FREECAD ASSEMBLY — COMPONENT RECIPES ("Assembly")

This assembly document has 5 components, labeled P0..P4 below (a component is one placed body or linked part). 5 of them carry a construction recipe — the FreeCAD feature program that regenerates the part from scratch, quoted from this document or its linked companion documents; the rest are supplied as boundary geometry only. No exploded tour is included for this assembly.
COMPONENT P0 — recipe-attached ("Backplane_DC", a linked part whose construction recipe lives in a companion FreeCAD document of the same project; that document's serialized recipe follows).
Construction recipe (the companion document, serialized — sketch geometry with constraints, then the solid features built on it; lengths are millimeters unless a unit is written):

FCSTD DOCUMENT  (FreeCAD 1.0R39109 (Git))
Label: Backplane_DC
License: All rights reserved
LicenseURL: https://en.wikipedia.org/wiki/All_rights_reserved
objects: Part::Feature×13, App::Part×11, PartDesign::CoordinateSystem×1, Sketcher::SketchObject×1
note: 16 computed .brp shape members not serialized (recipe doc carries the construction recipe); baked Part::Feature solids carry a one-line shape summary decoded from their .brp

FEATURE [Part::Feature] Part__Feature  label="MVQ-45H_____G_20130806_"
  shape: bbox 45.7 x 25.4 x 21.51 mm, 127 faces (baked)
FEATURE [Part::Feature] Part__Feature001  label="U\.1"
  Placement = pos=(-0.5,0,0) rot=(0,0,1;0rad)
  shape: bbox 57.37 x 25.98 x 2.346 mm, 78 faces (baked)
FEATURE [Part::Feature] Part__Feature002  label="PcB"
  Placement = pos=(-0.5,0,3.7) rot=(0,0,1;0rad)
  shape: bbox 42 x 22 x 1 mm, 8 faces (baked)
FEATURE [Part::Feature] Part__Feature003  label="pin.2"
  Placement = pos=(70.2231,-12.25,2.69484) rot=(0,1,0;3.14159rad)
  shape: bbox 1.8 x 1.8 x 9.8 mm, 12 faces (baked)
FEATURE [Part::Feature] Part__Feature004  label="pin.003"
  Placement = pos=(31.7232,-9.5,2.69484) rot=(0,1,0;3.14159rad)
  shape: bbox 1.8 x 1.8 x 9.8 mm, 12 faces (baked)
FEATURE [Part::Feature] Part__Feature005  label="pin.004"
  Placement = pos=(70.2231,-20.25,2.69484) rot=(0,1,0;3.14159rad)
  shape: bbox 1.8 x 1.8 x 9.8 mm, 12 faces (baked)
FEATURE [Part::Feature] Part__Feature006  label="pin.005"
  Placement = pos=(31.7232,-20.25,2.69484) rot=(0,1,0;3.14159rad)
  shape: bbox 1.8 x 1.8 x 9.8 mm, 12 faces (baked)
FEATURE [Part::Feature] Part__Feature007  label="79fa9e9c-a09d-11ed-8f45-a0cec80452fd_part"
  shape: bbox 8.4 x 14.4 x 13.5 mm, 26 faces (baked)
FEATURE [Part::Feature] Part__Feature008  label="79faa16c-a09d-11ed-8f45-a0cec80452fd_part"
  shape: bbox 1.1 x 1.1 x 2.6 mm, 12 faces (baked)
FEATURE [Part::Feature] Part__Feature009  label="79faa16c-a09d-11ed-8f45-a0cec80452fd_part001"
  shape: bbox 1.1 x 1.1 x 2.6 mm, 12 faces (baked)
FEATURE [Part::Feature] Part__Feature010  label="79faa16c-a09d-11ed-8f45-a0cec80452fd_part002"
  shape: bbox 1.1 x 1.1 x 2.6 mm, 12 faces (baked)
FEATURE [Part::Feature] Part__Feature011  label="79faa16c-a09d-11ed-8f45-a0cec80452fd_part003"
  shape: bbox 1.1 x 1.1 x 2.6 mm, 12 faces (baked)
FEATURE [App::Part] _9fa9e9c_a09d_11ed_8f45_a0cec80452fd  label="79fa9e9c-a09d-11ed-8f45-a0cec80452fd"
  Group = -> [Part__Feature007]
  Origin = -> Origin010
FEATURE [App::Part] _9faa16c_a09d_11ed_8f45_a0cec80452fd_part  label="79faa16c-a09d-11ed-8f45-a0cec80452fd_part004"
  Group = -> [Part__Feature008,Part__Feature009,Part__Feature010,Part__Feature011]
  Origin = -> Origin011
FEATURE [App::Part] _9faa16c_a09d_11ed_8f45_a0cec80452fd  label="79faa16c-a09d-11ed-8f45-a0cec80452fd"
  Group = -> [_9faa16c_a09d_11ed_8f45_a0cec80452fd_part]
  Origin = -> Origin012
FEATURE [App::Part] _9fa99c4_a09d_11ed_8f45_a0cec80452fd  label="79fa99c4-a09d-11ed-8f45-a0cec80452fd"
  Group = -> [_9fa9e9c_a09d_11ed_8f45_a0cec80452fd,_9faa16c_a09d_11ed_8f45_a0cec80452fd]
  Origin = -> Origin013
FEATURE [App::Part] CQ_assembly  label="J1_CQ assembly_5c03a136c24c"
  Group = -> [_9fa99c4_a09d_11ed_8f45_a0cec80452fd]
  Origin = -> Origin014
  Placement = pos=(88.1,2,0) rot=(0,0,1;1.5708rad)
FEATURE [App::Part] a1
  Group = -> [Part__Feature002,Part__Feature003,Part__Feature004,Part__Feature005,Part__Feature006]
  Origin = -> Origin008
FEATURE [App::Part] a2  label="U1_a2_d1753a728807"
  Group = -> [Part__Feature,Part__Feature001,a1]
  Origin = -> Origin009
  Placement = pos=(38.35,-48.52,0) rot=(0,0,1;0rad)
FEATURE [App::Part] Top_587c
  Group = -> [a2,CQ_assembly]
  Origin = -> Origin003
FEATURE [App::Part] Step_Models_587c
  Group = -> [Top_587c]
  Origin = -> Origin002
FEATURE [PartDesign::CoordinateSystem] Local_CS_587c
  AttacherType = Attacher::AttachEngine3D
  MapMode = 2
FEATURE [Part::Feature] Pcb_587c
  Placement = pos=(-40,140,0) rot=(0,0,1;0rad)
  shape: bbox 100 x 100 x 1.6 mm, 31 faces (baked)
FEATURE [Sketcher::SketchObject] PCB_Sketch_587c
  ArcFitTolerance = 1e-06
  FullyConstrained = false
  MakeInternals = false
  sketch-geometry (4):
    g0: LineSegment StartX=0 StartY=100 StartZ=0 EndX=100 EndY=100 EndZ=0
    g1: LineSegment StartX=100 StartY=100 StartZ=0 EndX=100 EndY=0 EndZ=0
    g2: LineSegment StartX=100 StartY=0 StartZ=0 EndX=0 EndY=0 EndZ=0
    g3: LineSegment StartX=0 StartY=0 StartZ=0 EndX=0 EndY=100 EndZ=0
  constraints (4):
    c: Coincident(g2,g3)
    c: Coincident(g0,g3)
    c: Coincident(g1,g2)
    c: Coincident(g0,g1)
FEATURE [App::Part] Board_Geoms_587c
  Group = -> [Pcb_587c,PCB_Sketch_587c]
  Origin = -> Origin
FEATURE [App::Part] Board_587c  label="Backplane_DC"
  Group = -> [Step_Models_587c,Local_CS_587c,Board_Geoms_587c]
  Origin = -> Origin001
COMPONENT P1 — recipe-attached ("Filter", a linked part whose construction recipe lives in a companion FreeCAD document of the same project; that document's serialized recipe follows).
Construction recipe (the companion document, serialized — sketch geometry with constraints, then the solid features built on it; lengths are millimeters unless a unit is written):

FCSTD DOCUMENT  (FreeCAD 1.0R39109 (Git))
Label: Filter
License: All rights reserved
LicenseURL: https://en.wikipedia.org/wiki/All_rights_reserved
objects: Part::Feature×93, App::Part×13, App::Link×3, PartDesign::CoordinateSystem×1, Sketcher::SketchObject×1
note: 96 computed .brp shape members not serialized (recipe doc carries the construction recipe); baked Part::Feature solids carry a one-line shape summary decoded from their .brp

FEATURE [App::Link] J2_1_276a3e213de9_2__ln_  label="J1_1_87cd8a65c9f8[2]"
  LinkPlacement = pos=(3.5,72.922,-1.6) rot=(0.707107,-0.707107,0;3.14159rad)
  LinkedObject = -> Shape002
  Placement = pos=(3.5,72.922,-1.6) rot=(0.707107,-0.707107,0;3.14159rad)
FEATURE [App::Link] L1_76080X203_858f18e4e3ac_ln_  label="L2_76080X203_3ff0c87f3d8e"
  LinkPlacement = pos=(104.05,0,20) rot=(0.57735,-0.57735,-0.57735;2.0944rad)
  LinkedObject = -> _6080X203
  Placement = pos=(104.05,0,20) rot=(0.57735,-0.57735,-0.57735;2.0944rad)
FEATURE [Part::Feature] Part__Feature  label="76080X203 Coil and Core"
  Placement = pos=(-13.4663,17.946,63.0505) rot=(0,0,1;0rad)
  shape: bbox 55.95 x 14.35 x 55.95 mm, 14 faces (baked)
FEATURE [Part::Feature] Part__Feature001  label="76080X203 Coil and Core001"
  Placement = pos=(-13.4663,17.946,63.0505) rot=(0,0,1;0rad)
  shape: bbox 3.314 x 63.05 x 20.62 mm, 22 faces (baked)
FEATURE [Part::Feature] Part__Feature002  label="76080X203 Coil and Core002"
  Placement = pos=(-13.4663,17.946,63.0505) rot=(0,0,1;0rad)
  shape: bbox 4.92 x 53.05 x 20.42 mm, 18 faces (baked)
FEATURE [Part::Feature] Part__Feature003  label="76080X203 Coil and Core003"
  Placement = pos=(-13.4663,17.946,63.0505) rot=(0,0,1;0rad)
  shape: bbox 6.495 x 53.05 x 20.09 mm, 18 faces (baked)
FEATURE [Part::Feature] Part__Feature004  label="76080X203 Coil and Core004"
  Placement = pos=(-13.4663,17.946,63.0505) rot=(0,0,1;0rad)
  shape: bbox 8.029 x 53.05 x 19.63 mm, 18 faces (baked)
FEATURE [Part::Feature] Part__Feature005  label="76080X203 Coil and Core005"
  Placement = pos=(-13.4663,17.946,63.0505) rot=(0,0,1;0rad)
  shape: bbox 9.513 x 53.05 x 19.05 mm, 18 faces (baked)
FEATURE [Part::Feature] Part__Feature006  label="76080X203 Coil and Core006"
  Placement = pos=(-13.4663,17.946,63.0505) rot=(0,0,1;0rad)
  shape: bbox 10.94 x 53.05 x 18.36 mm, 18 faces (baked)
FEATURE [Part::Feature] Part__Feature007  label="76080X203 Coil and Core007"
  Placement = pos=(-13.4663,17.946,63.0505) rot=(0,0,1;0rad)
  shape: bbox 12.29 x 53.05 x 17.54 mm, 18 faces (baked)
FEATURE [Part::Feature] Part__Feature008  label="76080X203 Coil and Core008"
  Placement = pos=(-13.4663,17.946,63.0505) rot=(0,0,1;0rad)
  shape: bbox 13.57 x 53.05 x 16.62 mm, 18 faces (baked)
FEATURE [Part::Feature] Part__Feature009  label="76080X203 Coil and Core009"
  Placement = pos=(-13.4663,17.946,63.0505) rot=(0,0,1;0rad)
  shape: bbox 14.77 x 53.05 x 15.59 mm, 18 faces (baked)
FEATURE [Part::Feature] Part__Feature010  label="76080X203 Coil and Core010"
  Placement = pos=(-13.4663,17.946,63.0505) rot=(0,0,1;0rad)
  shape: bbox 15.87 x 53.05 x 14.47 mm, 18 faces (baked)
FEATURE [Part::Feature] Part__Feature011  label="76080X203 Coil and Core011"
  Placement = pos=(-13.4663,17.946,63.0505) rot=(0,0,1;0rad)
  shape: bbox 16.87 x 53.05 x 13.25 mm, 18 faces (baked)
FEATURE [Part::Feature] Part__Feature012  label="76080X203 Coil and Core012"
  Placement = pos=(-13.4663,17.946,63.0505) rot=(0,0,1;0rad)
  shape: bbox 17.76 x 53.05 x 11.95 mm, 18 faces (baked)
FEATURE [Part::Feature] Part__Feature013  label="76080X203 Coil and Core013"
  Placement = pos=(-13.4663,17.946,63.0505) rot=(0,0,1;0rad)
  shape: bbox 18.55 x 53.05 x 10.58 mm, 18 faces (baked)
FEATURE [Part::Feature] Part__Feature014  label="76080X203 Coil and Core014"
  Placement = pos=(-13.4663,17.946,63.0505) rot=(0,0,1;0rad)
  shape: bbox 19.21 x 53.05 x 9.136 mm, 18 faces (baked)
FEATURE [Part::Feature] Part__Feature015  label="76080X203 Coil and Core015"
  Placement = pos=(-13.4663,17.946,63.0505) rot=(0,0,1;0rad)
  shape: bbox 19.76 x 53.05 x 7.638 mm, 18 faces (baked)
FEATURE [Part::Feature] Part__Feature016  label="76080X203 Coil and Core016"
  Placement = pos=(-13.4663,17.946,63.0505) rot=(0,0,1;0rad)
  shape: bbox 20.18 x 53.05 x 6.092 mm, 18 faces (baked)
FEATURE [Part::Feature] Part__Feature017  label="76080X203 Coil and Core017"
  Placement = pos=(-13.4663,17.946,63.0505) rot=(0,0,1;0rad)
  shape: bbox 20.48 x 53.05 x 4.508 mm, 18 faces (baked)
FEATURE [Part::Feature] Part__Feature018  label="76080X203 Coil and Core018"
  Placement = pos=(-13.4663,17.946,63.0505) rot=(0,0,1;0rad)
  shape: bbox 20.65 x 53.05 x 2.896 mm, 18 faces (baked)
FEATURE [Part::Feature] Part__Feature019  label="76080X203 Coil and Core019"
  Placement = pos=(-13.4663,17.946,63.0505) rot=(0,0,1;0rad)
  shape: bbox 20.69 x 53.05 x 1.265 mm, 18 faces (baked)
FEATURE [Part::Feature] Part__Feature020  label="76080X203 Coil and Core020"
  Placement = pos=(-13.4663,17.946,63.0505) rot=(0,0,1;0rad)
  shape: bbox 20.69 x 53.05 x 1.971 mm, 18 faces (baked)
FEATURE [Part::Feature] Part__Feature021  label="76080X203 Coil and Core021"
  Placement = pos=(-13.4663,17.946,63.0505) rot=(0,0,1;0rad)
  shape: bbox 20.59 x 53.05 x 3.595 mm, 18 faces (baked)
FEATURE [Part::Feature] Part__Feature022  label="76080X203 Coil and Core022"
  Placement = pos=(-13.4663,17.946,63.0505) rot=(0,0,1;0rad)
  shape: bbox 20.37 x 53.05 x 5.196 mm, 18 faces (baked)
FEATURE [Part::Feature] Part__Feature023  label="76080X203 Coil and Core023"
  Placement = pos=(-13.4663,17.946,63.0505) rot=(0,0,1;0rad)
  shape: bbox 20.02 x 53.05 x 6.765 mm, 18 faces (baked)
FEATURE [Part::Feature] Part__Feature024  label="76080X203 Coil and Core024"
  Placement = pos=(-13.4663,17.946,63.0505) rot=(0,0,1;0rad)
  shape: bbox 19.54 x 53.05 x 8.291 mm, 18 faces (baked)
FEATURE [Part::Feature] Part__Feature025  label="76080X203 Coil and Core025"
  Placement = pos=(-13.4663,17.946,63.0505) rot=(0,0,1;0rad)
  shape: bbox 18.94 x 53.05 x 9.766 mm, 18 faces (baked)
FEATURE [Part::Feature] Part__Feature026  label="76080X203 Coil and Core026"
  Placement = pos=(-13.4663,17.946,63.0505) rot=(0,0,1;0rad)
  shape: bbox 18.22 x 53.05 x 11.18 mm, 18 faces (baked)
FEATURE [Part::Feature] Part__Feature027  label="76080X203 Coil and Core027"
  Placement = pos=(-13.4663,17.946,63.0505) rot=(0,0,1;0rad)
  shape: bbox 17.39 x 53.05 x 12.52 mm, 18 faces (baked)
FEATURE [Part::Feature] Part__Feature028  label="76080X203 Coil and Core028"
  Placement = pos=(-13.4663,17.946,63.0505) rot=(0,0,1;0rad)
  shape: bbox 16.45 x 53.05 x 13.79 mm, 18 faces (baked)
FEATURE [Part::Feature] Part__Feature029  label="76080X203 Coil and Core029"
  Placement = pos=(-13.4663,17.946,63.0505) rot=(0,0,1;0rad)
  shape: bbox 15.4 x 53.05 x 14.96 mm, 18 faces (baked)
FEATURE [Part::Feature] Part__Feature030  label="76080X203 Coil and Core030"
  Placement = pos=(-13.4663,17.946,63.0505) rot=(0,0,1;0rad)
  shape: bbox 14.26 x 53.05 x 16.05 mm, 18 faces (baked)
FEATURE [Part::Feature] Part__Feature031  label="76080X203 Coil and Core031"
  Placement = pos=(-13.4663,17.946,63.0505) rot=(0,0,1;0rad)
  shape: bbox 13.03 x 53.05 x 17.03 mm, 18 faces (baked)
FEATURE [Part::Feature] Part__Feature032  label="76080X203 Coil and Core032"
  Placement = pos=(-13.4663,17.946,63.0505) rot=(0,0,1;0rad)
  shape: bbox 11.72 x 53.05 x 17.91 mm, 18 faces (baked)
FEATURE [Part::Feature] Part__Feature033  label="76080X203 Coil and Core033"
  Placement = pos=(-13.4663,17.946,63.0505) rot=(0,0,1;0rad)
  shape: bbox 10.33 x 53.05 x 18.67 mm, 18 faces (baked)
FEATURE [Part::Feature] Part__Feature034  label="76080X203 Coil and Core034"
  Placement = pos=(-13.4663,17.946,63.0505) rot=(0,0,1;0rad)
  shape: bbox 8.879 x 53.05 x 19.32 mm, 18 faces (baked)
FEATURE [Part::Feature] Part__Feature035  label="76080X203 Coil and Core035"
  Placement = pos=(-13.4663,17.946,63.0505) rot=(0,0,1;0rad)
  shape: bbox 7.372 x 53.05 x 19.84 mm, 18 faces (baked)
FEATURE [Part::Feature] Part__Feature036  label="76080X203 Coil and Core036"
  Placement = pos=(-13.4663,17.946,63.0505) rot=(0,0,1;0rad)
  shape: bbox 5.819 x 53.05 x 20.25 mm, 18 faces (baked)
FEATURE [Part::Feature] Part__Feature037  label="76080X203 Coil and Core037"
  Placement = pos=(-13.4663,17.946,63.0505) rot=(0,0,1;0rad)
  shape: bbox 4.229 x 53.05 x 20.52 mm, 18 faces (baked)
FEATURE [Part::Feature] Part__Feature038  label="76080X203 Coil and Core038"
  Placement = pos=(-13.4663,17.946,63.0505) rot=(0,0,1;0rad)
  shape: bbox 2.613 x 53.05 x 20.67 mm, 18 faces (baked)
FEATURE [Part::Feature] Part__Feature039  label="76080X203 Coil and Core039"
  Placement = pos=(-13.4663,17.946,63.0505) rot=(0,0,1;0rad)
  shape: bbox 0.9804 x 53.05 x 20.68 mm, 18 faces (baked)
FEATURE [Part::Feature] Part__Feature040  label="76080X203 Coil and Core040"
  Placement = pos=(-13.4663,17.946,63.0505) rot=(0,0,1;0rad)
  shape: bbox 2.254 x 53.05 x 20.68 mm, 18 faces (baked)
FEATURE [Part::Feature] Part__Feature041  label="76080X203 Coil and Core041"
  Placement = pos=(-13.4663,17.946,63.0505) rot=(0,0,1;0rad)
  shape: bbox 3.875 x 53.05 x 20.56 mm, 18 faces (baked)
FEATURE [Part::Feature] Part__Feature042  label="76080X203 Coil and Core042"
  Placement = pos=(-13.4663,17.946,63.0505) rot=(0,0,1;0rad)
  shape: bbox 5.472 x 53.05 x 20.32 mm, 18 faces (baked)
FEATURE [Part::Feature] Part__Feature043  label="76080X203 Coil and Core043"
  Placement = pos=(-13.4663,17.946,63.0505) rot=(0,0,1;0rad)
  shape: bbox 7.034 x 53.05 x 19.94 mm, 18 faces (baked)
FEATURE [Part::Feature] Part__Feature044  label="76080X203 Coil and Core044"
  Placement = pos=(-13.4663,17.946,63.0505) rot=(0,0,1;0rad)
  shape: bbox 8.552 x 53.05 x 19.44 mm, 18 faces (baked)
FEATURE [Part::Feature] Part__Feature045  label="76080X203 Coil and Core045"
  Placement = pos=(-13.4663,17.946,63.0505) rot=(0,0,1;0rad)
  shape: bbox 10.02 x 53.05 x 18.82 mm, 18 faces (baked)
FEATURE [Part::Feature] Part__Feature046  label="76080X203 Coil and Core046"
  Placement = pos=(-13.4663,17.946,63.0505) rot=(0,0,1;0rad)
  shape: bbox 11.42 x 53.05 x 18.09 mm, 18 faces (baked)
FEATURE [Part::Feature] Part__Feature047  label="76080X203 Coil and Core047"
  Placement = pos=(-13.4663,17.946,63.0505) rot=(0,0,1;0rad)
  shape: bbox 12.75 x 53.05 x 17.23 mm, 18 faces (baked)
FEATURE [Part::Feature] Part__Feature048  label="76080X203 Coil and Core048"
  Placement = pos=(-13.4663,17.946,63.0505) rot=(0,0,1;0rad)
  shape: bbox 14 x 53.05 x 16.27 mm, 18 faces (baked)
FEATURE [Part::Feature] Part__Feature049  label="76080X203 Coil and Core049"
  Placement = pos=(-13.4663,17.946,63.0505) rot=(0,0,1;0rad)
  shape: bbox 15.16 x 53.05 x 15.21 mm, 18 faces (baked)
FEATURE [Part::Feature] Part__Feature050  label="76080X203 Coil and Core050"
  Placement = pos=(-13.4663,17.946,63.0505) rot=(0,0,1;0rad)
  shape: bbox 16.23 x 53.05 x 14.05 mm, 18 faces (baked)
FEATURE [Part::Feature] Part__Feature051  label="76080X203 Coil and Core051"
  Placement = pos=(-13.4663,17.946,63.0505) rot=(0,0,1;0rad)
  shape: bbox 17.19 x 53.05 x 12.81 mm, 18 faces (baked)
FEATURE [Part::Feature] Part__Feature052  label="76080X203 Coil and Core052"
  Placement = pos=(-13.4663,17.946,63.0505) rot=(0,0,1;0rad)
  shape: bbox 18.05 x 53.05 x 11.48 mm, 18 faces (baked)
FEATURE [Part::Feature] Part__Feature053  label="76080X203 Coil and Core053"
  Placement = pos=(-13.4663,17.946,63.0505) rot=(0,0,1;0rad)
  shape: bbox 18.79 x 53.05 x 10.08 mm, 18 faces (baked)
FEATURE [Part::Feature] Part__Feature054  label="76080X203 Coil and Core054"
  Placement = pos=(-13.4663,17.946,63.0505) rot=(0,0,1;0rad)
  shape: bbox 19.42 x 53.05 x 8.621 mm, 18 faces (baked)
FEATURE [Part::Feature] Part__Feature055  label="76080X203 Coil and Core055"
  Placement = pos=(-13.4663,17.946,63.0505) rot=(0,0,1;0rad)
  shape: bbox 19.92 x 53.05 x 7.105 mm, 18 faces (baked)
FEATURE [Part::Feature] Part__Feature056  label="76080X203 Coil and Core056"
  Placement = pos=(-13.4663,17.946,63.0505) rot=(0,0,1;0rad)
  shape: bbox 20.3 x 53.05 x 5.545 mm, 18 faces (baked)
FEATURE [Part::Feature] Part__Feature057  label="76080X203 Coil and Core057"
  Placement = pos=(-13.4663,17.946,63.0505) rot=(0,0,1;0rad)
  shape: bbox 20.55 x 53.05 x 3.95 mm, 18 faces (baked)
FEATURE [Part::Feature] Part__Feature058  label="76080X203 Coil and Core058"
  Placement = pos=(-13.4663,17.946,63.0505) rot=(0,0,1;0rad)
  shape: bbox 20.68 x 53.05 x 2.33 mm, 18 faces (baked)
FEATURE [Part::Feature] Part__Feature059  label="76080X203 Coil and Core059"
  Placement = pos=(-13.4663,17.946,63.0505) rot=(0,0,1;0rad)
  shape: bbox 20.68 x 53.05 x 0.9044 mm, 18 faces (baked)
FEATURE [Part::Feature] Part__Feature060  label="76080X203 Coil and Core060"
  Placement = pos=(-13.4663,17.946,63.0505) rot=(0,0,1;0rad)
  shape: bbox 20.67 x 53.05 x 2.538 mm, 18 faces (baked)
FEATURE [Part::Feature] Part__Feature061  label="76080X203 Coil and Core061"
  Placement = pos=(-13.4663,17.946,63.0505) rot=(0,0,1;0rad)
  shape: bbox 20.53 x 53.05 x 4.155 mm, 18 faces (baked)
FEATURE [Part::Feature] Part__Feature062  label="76080X203 Coil and Core062"
  Placement = pos=(-13.4663,17.946,63.0505) rot=(0,0,1;0rad)
  shape: bbox 20.26 x 53.05 x 5.746 mm, 18 faces (baked)
FEATURE [Part::Feature] Part__Feature063  label="76080X203 Coil and Core063"
  Placement = pos=(-13.4663,17.946,63.0505) rot=(0,0,1;0rad)
  shape: bbox 19.87 x 53.05 x 7.301 mm, 18 faces (baked)
FEATURE [Part::Feature] Part__Feature064  label="76080X203 Coil and Core064"
  Placement = pos=(-13.4663,17.946,63.0505) rot=(0,0,1;0rad)
  shape: bbox 19.35 x 53.05 x 8.81 mm, 18 faces (baked)
FEATURE [Part::Feature] Part__Feature065  label="76080X203 Coil and Core065"
  Placement = pos=(-13.4663,17.946,63.0505) rot=(0,0,1;0rad)
  shape: bbox 18.7 x 53.05 x 10.26 mm, 18 faces (baked)
FEATURE [Part::Feature] Part__Feature066  label="76080X203 Coil and Core066"
  Placement = pos=(-13.4663,17.946,63.0505) rot=(0,0,1;0rad)
  shape: bbox 17.95 x 53.05 x 11.65 mm, 18 faces (baked)
FEATURE [Part::Feature] Part__Feature067  label="76080X203 Coil and Core067"
  Placement = pos=(-13.4663,17.946,63.0505) rot=(0,0,1;0rad)
  shape: bbox 17.07 x 53.05 x 12.97 mm, 18 faces (baked)
FEATURE [Part::Feature] Part__Feature068  label="76080X203 Coil and Core068"
  Placement = pos=(-13.4663,17.946,63.0505) rot=(0,0,1;0rad)
  shape: bbox 16.1 x 53.05 x 14.21 mm, 18 faces (baked)
FEATURE [Part::Feature] Part__Feature069  label="76080X203 Coil and Core069"
  Placement = pos=(-13.4663,17.946,63.0505) rot=(0,0,1;0rad)
  shape: bbox 15.02 x 53.05 x 15.35 mm, 18 faces (baked)
FEATURE [Part::Feature] Part__Feature070  label="76080X203 Coil and Core070"
  Placement = pos=(-13.4663,17.946,63.0505) rot=(0,0,1;0rad)
  shape: bbox 13.84 x 53.05 x 16.4 mm, 18 faces (baked)
FEATURE [Part::Feature] Part__Feature071  label="76080X203 Coil and Core071"
  Placement = pos=(-13.4663,17.946,63.0505) rot=(0,0,1;0rad)
  shape: bbox 12.58 x 53.05 x 17.35 mm, 18 faces (baked)
FEATURE [Part::Feature] Part__Feature072  label="76080X203 Coil and Core072"
  Placement = pos=(-13.4663,17.946,63.0505) rot=(0,0,1;0rad)
  shape: bbox 11.24 x 53.05 x 18.19 mm, 18 faces (baked)
FEATURE [Part::Feature] Part__Feature073  label="76080X203 Coil and Core073"
  Placement = pos=(-13.4663,17.946,63.0505) rot=(0,0,1;0rad)
  shape: bbox 9.833 x 53.05 x 18.91 mm, 18 faces (baked)
FEATURE [Part::Feature] Part__Feature074  label="76080X203 Coil and Core074"
  Placement = pos=(-13.4663,17.946,63.0505) rot=(0,0,1;0rad)
  shape: bbox 8.361 x 53.05 x 19.52 mm, 18 faces (baked)
FEATURE [Part::Feature] Part__Feature075  label="76080X203 Coil and Core075"
  Placement = pos=(-13.4663,17.946,63.0505) rot=(0,0,1;0rad)
  shape: bbox 6.837 x 53.05 x 20 mm, 18 faces (baked)
FEATURE [Part::Feature] Part__Feature076  label="76080X203 Coil and Core076"
  Placement = pos=(-13.4663,17.946,63.0505) rot=(0,0,1;0rad)
  shape: bbox 5.27 x 53.05 x 20.36 mm, 18 faces (baked)
FEATURE [Part::Feature] Part__Feature077  label="76080X203 Coil and Core077"
  Placement = pos=(-13.4663,17.946,63.0505) rot=(0,0,1;0rad)
  shape: bbox 3.67 x 53.05 x 20.59 mm, 18 faces (baked)
FEATURE [Part::Feature] Part__Feature078  label="76080X203 Coil and Core078"
  Placement = pos=(-13.4663,17.946,63.0505) rot=(0,0,1;0rad)
  shape: bbox 1.881 x 63.05 x 20.92 mm, 22 faces (baked)
FEATURE [Part::Feature] Part__Feature079  label="76080X203 Coil and Core079"
  Placement = pos=(-13.4663,17.946,63.0505) rot=(0,0,1;0rad)
  shape: bbox 55.95 x 14.35 x 55.95 mm, 14 faces (baked)
FEATURE [Part::Feature] Part__Feature080  label="76080X203 Coil and Core080"
  Placement = pos=(-13.4663,17.946,63.0505) rot=(0,0,1;0rad)
  shape: bbox 55.95 x 14.35 x 55.95 mm, 14 faces (baked)
FEATURE [Part::Feature] Part__Feature081  label="070-7778_65mm10"
  Placement = pos=(-13.4663,39.296,63.0505) rot=(1,-0.0006,0.0006;1.5708rad)
  shape: bbox 63.86 x 10.5 x 66.59 mm, 131 faces (baked)
FEATURE [Part::Feature] Part__Feature082  label="070-7778_65mm011"
  Placement = pos=(-13.4663,-17.754,63.0505) rot=(-0.000425,0.707107,0.707107;3.14074rad)
  shape: bbox 63.86 x 10.5 x 66.59 mm, 131 faces (baked)
FEATURE [Part::Feature] Part__Feature083  label="4mm lock nut_94645A101"
  Placement = pos=(-13.4663,-13.854,63.0505) rot=(1,0,0.0006;3.14159rad)
  shape: bbox 7.082 x 0.6047 x 7.082 mm, 6 faces (baked)
FEATURE [Part::Feature] Part__Feature084  label="4mm lock nut_94645A102"
  Placement = pos=(-13.4663,-13.854,63.0505) rot=(1,0,0.0006;3.14159rad)
  shape: bbox 8.084 x 5.147 x 8.084 mm, 47 faces (baked)
FEATURE [Part::Feature] Part__Feature085  label="4mm OD 65mm long_screw_91290A083"
  Placement = pos=(-13.4663,4.39598,63.0505) rot=(-1,0,0;1.5708rad)
  shape: bbox 7.001 x 70.05 x 7.001 mm, 88 faces (baked)
FEATURE [Part::Feature] Part__Feature086  label="b59e4a84-a09d-11ed-8f45-a0cec80452fd_part"
  shape: bbox 16.8 x 24.15 x 19.6 mm, 26 faces (baked)
FEATURE [Part::Feature] Part__Feature087  label="b59e4d5e-a09d-11ed-8f45-a0cec80452fd_part"
  shape: bbox 2.1 x 2.1 x 4.6 mm, 8 faces (baked)
FEATURE [Part::Feature] Part__Feature088  label="b59e4d5e-a09d-11ed-8f45-a0cec80452fd_part001"
  shape: bbox 2.1 x 2.1 x 4.6 mm, 8 faces (baked)
FEATURE [App::Link] R1_R_Axial_DIN0617_L170mm_D60mm_P2540mm_Horizontal_f8ce5df8ddfd_ln_  label="R2_R_Axial_DIN0617_L170mm_D60mm_P2540mm_Horizontal_76c3f4d7f436"
  LinkPlacement = pos=(91,91.5,0) rot=(0,0,-1;1.5708rad)
  LinkedObject = -> Shape
  Placement = pos=(91,91.5,0) rot=(0,0,-1;1.5708rad)
FEATURE [Part::Feature] Shape  label="R1_R_Axial_DIN0617_L170mm_D60mm_P2540mm_Horizontal_f8ce5df8ddfd"
  Placement = pos=(91,31.1,0) rot=(0,0,-1;1.5708rad)
  shape: bbox 6.494 x 26.46 x 9.247 mm, 17 faces (baked)
FEATURE [Part::Feature] Shape001  label="C1_C_Rect_L265mm_W115mm_P2250mm_MKS4_fe84fe0ab4d3"
  Placement = pos=(75.6,60.95,0) rot=(0,0,-1;1.5708rad)
  shape: bbox 11.5 x 26.5 x 22.9 mm, 22 faces (baked)
FEATURE [Part::Feature] Shape002  label="J2_1_276a3e213de9[2]"
  Placement = pos=(3.5,11.962,-1.6) rot=(0.707107,-0.707107,0;3.14159rad)
  shape: bbox 7 x 4.98 x 4.98 mm, 13 faces (baked)
FEATURE [App::Part] Bot_ee73
  Group = -> [Shape002,J2_1_276a3e213de9_2__ln_]
  Origin = -> Origin004
FEATURE [App::Part] _6080X203_Coil_and_Core  label="76080X203 Coil and Core081"
  Group = -> [Part__Feature,Part__Feature001,Part__Feature002,Part__Feature003,Part__Feature004,Part__Feature005,Part__Feature006,Part__Feature007,Part__Feature008,Part__Feature009,Part__Feature010,Part__Feature011,Part__Feature012,Part__Feature013,Part__Feature014,Part__Feature015,Part__Feature016,Part__Feature017,Part__Feature018,Part__Feature019,Part__Feature020,Part__Feature021,Part__Feature022,+58 more]
  Origin = -> Origin008
FEATURE [App::Part] _mm_lock_nut_94645A101  label="4mm lock nut_94645A103"
  Group = -> [Part__Feature083,Part__Feature084]
  Origin = -> Origin009
FEATURE [App::Part] _6080X203  label="L1_76080X203_858f18e4e3ac"
  Group = -> [_6080X203_Coil_and_Core,Part__Feature081,Part__Feature082,_mm_lock_nut_94645A101,Part__Feature085]
  Origin = -> Origin010
  Placement = pos=(104.05,72.5,20) rot=(0.57735,-0.57735,-0.57735;2.0944rad)
FEATURE [App::Part] b59e4a84_a09d_11ed_8f45_a0cec80452fd  label="b59e4a84-a09d-11ed-8f45-a0cec80452fd"
  Group = -> [Part__Feature086]
  Origin = -> Origin011
FEATURE [App::Part] b59e4d5e_a09d_11ed_8f45_a0cec80452fd_part  label="b59e4d5e-a09d-11ed-8f45-a0cec80452fd_part002"
  Group = -> [Part__Feature087,Part__Feature088]
  Origin = -> Origin012
FEATURE [App::Part] b59e4d5e_a09d_11ed_8f45_a0cec80452fd  label="b59e4d5e-a09d-11ed-8f45-a0cec80452fd"
  Group = -> [b59e4d5e_a09d_11ed_8f45_a0cec80452fd_part]
  Origin = -> Origin013
FEATURE [App::Part] b59e462e_a09d_11ed_8f45_a0cec80452fd  label="b59e462e-a09d-11ed-8f45-a0cec80452fd"
  Group = -> [b59e4a84_a09d_11ed_8f45_a0cec80452fd,b59e4d5e_a09d_11ed_8f45_a0cec80452fd]
  Origin = -> Origin014
FEATURE [App::Part] CQ_assembly  label="J3_CQ assembly_8f48752883f5"
  Group = -> [b59e462e_a09d_11ed_8f45_a0cec80452fd]
  Origin = -> Origin015
  Placement = pos=(84.0925,45.85,0) rot=(0,0,1;1.5708rad)
FEATURE [App::Part] Top_ee73
  Group = -> [_6080X203,L1_76080X203_858f18e4e3ac_ln_,Shape,R1_R_Axial_DIN0617_L170mm_D60mm_P2540mm_Horizontal_f8ce5df8ddfd_ln_,Shape001,CQ_assembly]
  Origin = -> Origin003
FEATURE [App::Part] Step_Models_ee73
  Group = -> [Top_ee73,Bot_ee73]
  Origin = -> Origin002
FEATURE [PartDesign::CoordinateSystem] Local_CS_ee73
  AttacherType = Attacher::AttachEngine3D
  MapMode = 2
FEATURE [Part::Feature] Pcb_ee73
  Placement = pos=(-40,160,0) rot=(0,0,1;0rad)
  shape: bbox 100 x 100 x 1.6 mm, 44 faces (baked)
FEATURE [Sketcher::SketchObject] PCB_Sketch_ee73
  ArcFitTolerance = 1e-06
  FullyConstrained = false
  MakeInternals = false
  sketch-geometry (4):
    g0: LineSegment StartX=0 StartY=100 StartZ=0 EndX=100 EndY=100 EndZ=0
    g1: LineSegment StartX=100 StartY=100 StartZ=0 EndX=100 EndY=0 EndZ=0
    g2: LineSegment StartX=100 StartY=0 StartZ=0 EndX=0 EndY=0 EndZ=0
    g3: LineSegment StartX=0 StartY=0 StartZ=0 EndX=0 EndY=100 EndZ=0
  constraints (4):
    c: Coincident(g2,g3)
    c: Coincident(g0,g3)
    c: Coincident(g1,g2)
    c: Coincident(g0,g1)
FEATURE [App::Part] Board_Geoms_ee73
  Group = -> [Pcb_ee73,PCB_Sketch_ee73]
  Origin = -> Origin
FEATURE [App::Part] Board_ee73  label="Filter"
  Group = -> [Step_Models_ee73,Local_CS_ee73,Board_Geoms_ee73]
  Origin = -> Origin001
COMPONENT P2 — recipe-attached ("HalfBridge_SiC1", a linked part whose construction recipe lives in a companion FreeCAD document of the same project; that document's serialized recipe follows).
Construction recipe (the companion document, serialized — sketch geometry with constraints, then the solid features built on it; lengths are millimeters unless a unit is written):

FCSTD DOCUMENT  (FreeCAD 1.0R39109 (Git))
Label: HalfBridge_SiC
License: All rights reserved
LicenseURL: https://en.wikipedia.org/wiki/All_rights_reserved
objects: App::Link×105, Part::Feature×46, App::Part×15, PartDesign::CoordinateSystem×1, Sketcher::SketchObject×1
note: 49 computed .brp shape members not serialized (recipe doc carries the construction recipe); baked Part::Feature solids carry a one-line shape summary decoded from their .brp

FEATURE [PartDesign::CoordinateSystem] Local_CS_ed05
  AttacherType = Attacher::AttachEngine3D
  MapMode = 2
FEATURE [Part::Feature] Pcb_ed05
  Placement = pos=(-39.5,140.5,0) rot=(0,0,1;0rad)
  shape: bbox 100 x 100 x 1.6 mm, 113 faces (baked)
FEATURE [Sketcher::SketchObject] PCB_Sketch_ed05
  ArcFitTolerance = 1e-06
  FullyConstrained = false
  MakeInternals = false
  sketch-geometry (28):
    g0: LineSegment StartX=17.542 StartY=39.29 StartZ=0 EndX=18.542 EndY=39.29 EndZ=0
    g1: LineSegment StartX=18.542 StartY=39.29 StartZ=0 EndX=18.542 EndY=29.29 EndZ=0
    g2: LineSegment StartX=18.542 StartY=29.29 StartZ=0 EndX=17.542 EndY=29.29 EndZ=0
    g3: LineSegment StartX=17.542 StartY=29.29 StartZ=0 EndX=17.542 EndY=39.29 EndZ=0
    g4: LineSegment StartX=36.399 StartY=40.662 StartZ=0 EndX=45.383 EndY=40.662 EndZ=0
    g5: LineSegment StartX=45.383 StartY=40.662 StartZ=0 EndX=45.383 EndY=39.662 EndZ=0
    g6: LineSegment StartX=45.383 StartY=39.662 StartZ=0 EndX=36.399 EndY=39.662 EndZ=0
    g7: LineSegment StartX=36.399 StartY=39.662 StartZ=0 EndX=36.399 EndY=40.662 EndZ=0
    g8: LineSegment StartX=47.768 StartY=91.487 StartZ=0 EndX=48.514 EndY=91.487 EndZ=0
    g9: LineSegment StartX=48.514 StartY=91.487 StartZ=0 EndX=48.514 EndY=59.389 EndZ=0
    g10: LineSegment StartX=48.514 StartY=59.389 StartZ=0 EndX=47.768 EndY=59.389 EndZ=0
    g11: LineSegment StartX=47.768 StartY=59.389 StartZ=0 EndX=47.768 EndY=91.487 EndZ=0
    g12: LineSegment StartX=17.968 StartY=23.7 StartZ=0 EndX=74.68 EndY=23.7 EndZ=0
    g13: LineSegment StartX=74.68 StartY=23.7 StartZ=0 EndX=74.68 EndY=22.7 EndZ=0
    g14: LineSegment StartX=74.68 StartY=22.7 StartZ=0 EndX=17.968 EndY=22.7 EndZ=0
    g15: LineSegment StartX=17.968 StartY=22.7 StartZ=0 EndX=17.968 EndY=23.7 EndZ=0
    g16: LineSegment StartX=0 StartY=100 StartZ=0 EndX=100 EndY=100 EndZ=0
    g17: LineSegment StartX=100 StartY=100 StartZ=0 EndX=100 EndY=0 EndZ=0
    g18: LineSegment StartX=100 StartY=0 StartZ=0 EndX=0 EndY=0 EndZ=0
    g19: LineSegment StartX=0 StartY=0 StartZ=0 EndX=0 EndY=100 EndZ=0
    g20: LineSegment StartX=18.05 StartY=15.208 StartZ=0 EndX=19.05 EndY=15.208 EndZ=0
    g21: LineSegment StartX=19.05 StartY=15.208 StartZ=0 EndX=19.05 EndY=8.7 EndZ=0
    g22: LineSegment StartX=19.05 StartY=8.7 StartZ=0 EndX=18.05 EndY=8.7 EndZ=0
    g23: LineSegment StartX=18.05 StartY=8.7 StartZ=0 EndX=18.05 EndY=15.208 EndZ=0
    g24: LineSegment StartX=15.764 StartY=29.4 StartZ=0 EndX=16.764 EndY=29.4 EndZ=0
    g25: LineSegment StartX=16.764 StartY=29.4 StartZ=0 EndX=16.764 EndY=16.9 EndZ=0
    g26: LineSegment StartX=16.764 StartY=16.9 StartZ=0 EndX=15.764 EndY=16.9 EndZ=0
    g27: LineSegment StartX=15.764 StartY=16.9 StartZ=0 EndX=15.764 EndY=29.4 EndZ=0
  constraints (28):
    c: Coincident(g18,g19)
    c: Coincident(g16,g19)
    c: Coincident(g26,g27)
    c: Coincident(g24,g27)
    c: Coincident(g25,g26)
    c: Coincident(g24,g25)
    c: Coincident(g2,g3)
    c: Coincident(g0,g3)
    c: Coincident(g14,g15)
    c: Coincident(g12,g15)
    c: Coincident(g22,g23)
    c: Coincident(g20,g23)
    c: Coincident(g1,g2)
    c: Coincident(g0,g1)
    c: Coincident(g21,g22)
    c: Coincident(g20,g21)
    c: Coincident(g6,g7)
    c: Coincident(g4,g7)
    c: Coincident(g5,g6)
    c: Coincident(g4,g5)
    c: Coincident(g10,g11)
    c: Coincident(g8,g11)
    c: Coincident(g9,g10)
    c: Coincident(g8,g9)
    c: Coincident(g13,g14)
    c: Coincident(g12,g13)
    c: Coincident(g17,g18)
    c: Coincident(g16,g17)
FEATURE [App::Part] Board_Geoms_ed05
  Group = -> [Pcb_ed05,PCB_Sketch_ed05]
  Origin = -> Origin
FEATURE [Part::Feature] Shape  label="U5_SOIC-16W_7.5x10.3mm_P1.27mm_noPin12_13_606f1c37d418"
  Placement = pos=(18,23.3,0) rot=(0,0,1;0rad)
  shape: bbox 10.3 x 10.3 x 2.75 mm, 256 faces (baked)
FEATURE [Part::Feature] Shape001  label="D6_D_SOD_123_86f777a7cf57"
  Placement = pos=(31.3,17.35,0) rot=(0,0,-1;1.5708rad)
  shape: bbox 1.6 x 3.8 x 1.25 mm, 67 faces (baked)
FEATURE [Part::Feature] Shape002  label="R9_R_0603_1608Metric_fe9d9f34c5f9"
  Placement = pos=(9.9875,27.2,0) rot=(0,0,1;0rad)
  shape: bbox 1.6 x 0.8 x 0.45 mm, 26 faces (baked)
FEATURE [App::Link] D6_D_SOD_123_86f777a7cf57_ln_  label="D5_D_SOD_123_75c73be4f775"
  LinkPlacement = pos=(31.3,29.9,0) rot=(0,0,1;1.5708rad)
  LinkedObject = -> Shape001
  Placement = pos=(31.3,29.9,0) rot=(0,0,1;1.5708rad)
FEATURE [Part::Feature] Shape003  label="C15_C_0603_1608Metric_09ddd0478757"
  Placement = pos=(13.5,16.1,0) rot=(0,0,-1;1.5708rad)
  shape: bbox 0.8 x 1.6 x 0.8 mm, 28 faces (baked)
FEATURE [App::Link] C15_C_0603_1608Metric_09ddd0478757_ln_  label="C33_C_0603_1608Metric_74bc470caa33"
  LinkPlacement = pos=(9.3,80.8715,0) rot=(0,0,1;1.5708rad)
  LinkedObject = -> Shape003
  Placement = pos=(9.3,80.8715,0) rot=(0,0,1;1.5708rad)
FEATURE [Part::Feature] Shape004  label="D3_LED_0603_1608Metric_70bb5031e2ff"
  Placement = pos=(4.7,31.775,0) rot=(0,0,-1;1.5708rad)
  shape: bbox 0.8 x 1.6 x 1.1 mm, 50 faces (baked)
FEATURE [Part::Feature] Shape005  label="C38_C_0805_2012Metric_74cbd35bff10"
  Placement = pos=(6.655,73.284,0) rot=(0,0,1;0rad)
  shape: bbox 2 x 1.25 x 1.25 mm, 28 faces (baked)
FEATURE [App::Link] R9_R_0603_1608Metric_fe9d9f34c5f9_ln_  label="R33_R_0603_1608Metric_ea8747869db3"
  LinkPlacement = pos=(22.7,83.4115,0) rot=(0,0,1;1.5708rad)
  LinkedObject = -> Shape002
  Placement = pos=(22.7,83.4115,0) rot=(0,0,1;1.5708rad)
FEATURE [App::Link] C15_C_0603_1608Metric_09ddd0478757_ln_001  label="C22_C_0603_1608Metric_3b7886544036"
  LinkPlacement = pos=(25.65,28.3,0) rot=(0,0,1;0rad)
  LinkedObject = -> Shape003
  Placement = pos=(25.65,28.3,0) rot=(0,0,1;0rad)
FEATURE [Part::Feature] Part__Feature  label="CAS_c_12B"
  Placement = pos=(0,-2.4,-3e-16) rot=(0,0,1;0rad)
  shape: bbox 5.4 x 2.5 x 4.2 mm, 71 faces (baked)
FEATURE [Part::Feature] Part__Feature001  label="1 pole_s"
  Placement = pos=(0.3,-0.6,-3e-16) rot=(0,0,1;0rad)
  shape: bbox 0.6 x 0.6 x 0.7 mm, 14 faces (baked)
FEATURE [App::Part] CAS_120B1  label="SW1_CAS-120B1_eba1f44a47b7[2]"
  Group = -> [Part__Feature,Part__Feature001]
  Origin = -> Origin008
  Placement = pos=(29.242,83.058,2.5) rot=(0.57735,-0.57735,-0.57735;2.0944rad)
FEATURE [App::Link] R9_R_0603_1608Metric_fe9d9f34c5f9_ln_001  label="R14_R_0603_1608Metric_f9b5c031c635"
  LinkPlacement = pos=(28.1,36.5,0) rot=(0,0,1;1.5708rad)
  LinkedObject = -> Shape002
  Placement = pos=(28.1,36.5,0) rot=(0,0,1;1.5708rad)
FEATURE [App::Link] R9_R_0603_1608Metric_fe9d9f34c5f9_ln_002  label="R8_R_0603_1608Metric_fcb6b5fbbfd0"
  LinkPlacement = pos=(10,28.7,0) rot=(0,0,1;0rad)
  LinkedObject = -> Shape002
  Placement = pos=(10,28.7,0) rot=(0,0,1;0rad)
FEATURE [App::Link] C15_C_0603_1608Metric_09ddd0478757_ln_002  label="C45_C_0603_1608Metric_6c9f5762c5a1"
  LinkPlacement = pos=(36.9,16.256,0) rot=(0,0,1;1.5708rad)
  LinkedObject = -> Shape003
  Placement = pos=(36.9,16.256,0) rot=(0,0,1;1.5708rad)
FEATURE [App::Link] C38_C_0805_2012Metric_74cbd35bff10_ln_  label="C24_C_0805_2012Metric_4c91d95a9eef"
  LinkPlacement = pos=(25.7,8.7,0) rot=(0,0,1;3.14159rad)
  LinkedObject = -> Shape005
  Placement = pos=(25.7,8.7,0) rot=(0,0,1;3.14159rad)
FEATURE [Part::Feature] Shape006  label="U10_SOT_23_6_8cf1dc40b667"
  Placement = pos=(21.85,68.3115,0) rot=(0,0,1;3.14159rad)
  shape: bbox 2.8 x 2.9 x 1.55 mm, 124 faces (baked)
FEATURE [App::Link] C15_C_0603_1608Metric_09ddd0478757_ln_003  label="C21_C_0603_1608Metric_d16c1e161e8d"
  LinkPlacement = pos=(25.62,18.5,0) rot=(0,0,1;3.14159rad)
  LinkedObject = -> Shape003
  Placement = pos=(25.62,18.5,0) rot=(0,0,1;3.14159rad)
FEATURE [App::Link] C15_C_0603_1608Metric_09ddd0478757_ln_004  label="C42_C_0603_1608Metric_20bf4b114d9d"
  LinkPlacement = pos=(25.1,68.1115,0) rot=(0,0,1;1.5708rad)
  LinkedObject = -> Shape003
  Placement = pos=(25.1,68.1115,0) rot=(0,0,1;1.5708rad)
FEATURE [App::Link] C38_C_0805_2012Metric_74cbd35bff10_ln_001  label="C18_C_0805_2012Metric_4df3bd6c3c50"
  LinkPlacement = pos=(25.7,33.1,0) rot=(0,0,1;3.14159rad)
  LinkedObject = -> Shape005
  Placement = pos=(25.7,33.1,0) rot=(0,0,1;3.14159rad)
FEATURE [App::Link] U10_SOT_23_6_8cf1dc40b667_ln_  label="U11_SOT_23_6_c211cb7acc4a"
  LinkPlacement = pos=(21.85,58.1515,0) rot=(0,0,1;3.14159rad)
  LinkedObject = -> Shape006
  Placement = pos=(21.85,58.1515,0) rot=(0,0,1;3.14159rad)
FEATURE [App::Link] R9_R_0603_1608Metric_fe9d9f34c5f9_ln_003  label="R15_R_0603_1608Metric_55e85660f00f"
  LinkPlacement = pos=(22.6,36.1,0) rot=(0,0,-1;1.5708rad)
  LinkedObject = -> Shape002
  Placement = pos=(22.6,36.1,0) rot=(0,0,-1;1.5708rad)
FEATURE [Part::Feature] Shape007  label="R21_R_0805_2012Metric_4eff570911b6"
  Placement = pos=(34.3,28.2,0) rot=(0,0,1;0rad)
  shape: bbox 2 x 1.2 x 0.45 mm, 26 faces (baked)
FEATURE [App::Link] C15_C_0603_1608Metric_09ddd0478757_ln_005  label="C34_C_0603_1608Metric_836b7f75df63"
  LinkPlacement = pos=(9.5,60.3715,0) rot=(0,0,1;1.5708rad)
  LinkedObject = -> Shape003
  Placement = pos=(9.5,60.3715,0) rot=(0,0,1;1.5708rad)
FEATURE [App::Link] C38_C_0805_2012Metric_74cbd35bff10_ln_002  label="C39_C_0805_2012Metric_4739b33e3560"
  LinkPlacement = pos=(6.655,83.9115,0) rot=(0,0,1;0rad)
  LinkedObject = -> Shape005
  Placement = pos=(6.655,83.9115,0) rot=(0,0,1;0rad)
FEATURE [App::Link] R9_R_0603_1608Metric_fe9d9f34c5f9_ln_004  label="R16_R_0603_1608Metric_5e29ad9bbd6c"
  LinkPlacement = pos=(29.7,13.3,0) rot=(0,0,-1;1.5708rad)
  LinkedObject = -> Shape002
  Placement = pos=(29.7,13.3,0) rot=(0,0,-1;1.5708rad)
FEATURE [App::Link] C15_C_0603_1608Metric_09ddd0478757_ln_006  label="C6_C_0603_1608Metric_47ec0beeeb7c"
  LinkPlacement = pos=(36.576,85.598,0) rot=(0,0,1;0rad)
  LinkedObject = -> Shape003
  Placement = pos=(36.576,85.598,0) rot=(0,0,1;0rad)
FEATURE [App::Link] D3_LED_0603_1608Metric_70bb5031e2ff_ln_  label="D1_LED_0603_1608Metric_117d22e4d741"
  LinkPlacement = pos=(3.1,9.525,0) rot=(0,0,1;1.5708rad)
  LinkedObject = -> Shape004
  Placement = pos=(3.1,9.525,0) rot=(0,0,1;1.5708rad)
FEATURE [Part::Feature] Shape008  label="U3_SOT_23_5_e32904241429"
  Placement = pos=(34.37,62.7015,0) rot=(0,0,1;0rad)
  shape: bbox 2.8 x 2.9 x 1.55 mm, 109 faces (baked)
FEATURE [App::Link] C38_C_0805_2012Metric_74cbd35bff10_ln_003  label="C35_C_0805_2012Metric_12818f10c88b"
  LinkPlacement = pos=(7.5,67.9115,0) rot=(0,0,1;3.14159rad)
  LinkedObject = -> Shape005
  Placement = pos=(7.5,67.9115,0) rot=(0,0,1;3.14159rad)
FEATURE [Part::Feature] Shape009  label="U7_SOT_23_ed8fd63cd947"
  Placement = pos=(25.3625,36.5,0) rot=(0,0,1;3.14159rad)
  shape: bbox 2.5 x 3 x 1.2 mm, 76 faces (baked)
FEATURE [Part::Feature] Shape010  label="C5_C_2220_5750Metric_40789e461117"
  Placement = pos=(71.498,23.622,0) rot=(0,0,-1;1.5708rad)
  shape: bbox 5 x 5.7 x 2.9 mm, 28 faces (baked)
FEATURE [App::Link] R9_R_0603_1608Metric_fe9d9f34c5f9_ln_005  label="R29_R_0603_1608Metric_c415b56a8a35"
  LinkPlacement = pos=(13.655,63.4115,0) rot=(0,0,1;1.5708rad)
  LinkedObject = -> Shape002
  Placement = pos=(13.655,63.4115,0) rot=(0,0,1;1.5708rad)
FEATURE [App::Link] R9_R_0603_1608Metric_fe9d9f34c5f9_ln_006  label="R27_R_0603_1608Metric_6ecdd8c441b3"
  LinkPlacement = pos=(13.3,73.9115,0) rot=(0,0,1;1.5708rad)
  LinkedObject = -> Shape002
  Placement = pos=(13.3,73.9115,0) rot=(0,0,1;1.5708rad)
FEATURE [App::Link] R9_R_0603_1608Metric_fe9d9f34c5f9_ln_007  label="R30_R_0603_1608Metric_3d9fcfb98980"
  LinkPlacement = pos=(18.7,78.4115,0) rot=(0,0,1;1.5708rad)
  LinkedObject = -> Shape002
  Placement = pos=(18.7,78.4115,0) rot=(0,0,1;1.5708rad)
FEATURE [App::Link] C15_C_0603_1608Metric_09ddd0478757_ln_007  label="C41_C_0603_1608Metric_8a3fc6cb6ce4"
  LinkPlacement = pos=(25.1,78.4115,0) rot=(0,0,1;1.5708rad)
  LinkedObject = -> Shape003
  Placement = pos=(25.1,78.4115,0) rot=(0,0,1;1.5708rad)
FEATURE [App::Link] C5_C_2220_5750Metric_40789e461117_ln_  label="C3_C_2220_5750Metric_0b14797a19db"
  LinkPlacement = pos=(59.498,23.622,0) rot=(0,0,-1;1.5708rad)
  LinkedObject = -> Shape010
  Placement = pos=(59.498,23.622,0) rot=(0,0,-1;1.5708rad)
FEATURE [App::Link] R21_R_0805_2012Metric_4eff570911b6_ln_  label="R19_R_0805_2012Metric_5467f9f4486e"
  LinkPlacement = pos=(34.3,32.2,0) rot=(0,0,1;0rad)
  LinkedObject = -> Shape007
  Placement = pos=(34.3,32.2,0) rot=(0,0,1;0rad)
FEATURE [App::Link] C15_C_0603_1608Metric_09ddd0478757_ln_008  label="C43_C_0603_1608Metric_b35c248b52c4"
  LinkPlacement = pos=(25.1,58.1115,0) rot=(0,0,1;1.5708rad)
  LinkedObject = -> Shape003
  Placement = pos=(25.1,58.1115,0) rot=(0,0,1;1.5708rad)
FEATURE [App::Link] R21_R_0805_2012Metric_4eff570911b6_ln_001  label="R3_R_0805_2012Metric_ab16afa742b3"
  LinkPlacement = pos=(44.564,16.278,0) rot=(0,0,1;1.5708rad)
  LinkedObject = -> Shape007
  Placement = pos=(44.564,16.278,0) rot=(0,0,1;1.5708rad)
FEATURE [App::Link] R21_R_0805_2012Metric_4eff570911b6_ln_002  label="R10_R_0805_2012Metric_e1b373d5c9e0"
  LinkPlacement = pos=(8.1,18.67,0) rot=(0,0,-1;1.5708rad)
  LinkedObject = -> Shape007
  Placement = pos=(8.1,18.67,0) rot=(0,0,-1;1.5708rad)
FEATURE [App::Link] D3_LED_0603_1608Metric_70bb5031e2ff_ln_001  label="D2_LED_0603_1608Metric_72f350e39bfe"
  LinkPlacement = pos=(4.7,35.5,0) rot=(0,0,-1;1.5708rad)
  LinkedObject = -> Shape004
  Placement = pos=(4.7,35.5,0) rot=(0,0,-1;1.5708rad)
FEATURE [App::Link] R9_R_0603_1608Metric_fe9d9f34c5f9_ln_008  label="R32_R_0603_1608Metric_bd0168379d35"
  LinkPlacement = pos=(18.7,58.1115,0) rot=(0,0,1;1.5708rad)
  LinkedObject = -> Shape002
  Placement = pos=(18.7,58.1115,0) rot=(0,0,1;1.5708rad)
FEATURE [App::Link] C38_C_0805_2012Metric_74cbd35bff10_ln_004  label="C40_C_0805_2012Metric_1a8242036e69"
  LinkPlacement = pos=(6.7,63.1115,0) rot=(0,0,1;0rad)
  LinkedObject = -> Shape005
  Placement = pos=(6.7,63.1115,0) rot=(0,0,1;0rad)
FEATURE [App::Link] R21_R_0805_2012Metric_4eff570911b6_ln_003  label="R40_R_0805_2012Metric_1fb8d6502ab2"
  LinkPlacement = pos=(20.574,16.04,0) rot=(0,0,-1;1.5708rad)
  LinkedObject = -> Shape007
  Placement = pos=(20.574,16.04,0) rot=(0,0,-1;1.5708rad)
FEATURE [App::Link] C15_C_0603_1608Metric_09ddd0478757_ln_009  label="C20_C_0603_1608Metric_5de1c2e82c4e"
  LinkPlacement = pos=(25.62,21.1,0) rot=(0,0,1;0rad)
  LinkedObject = -> Shape003
  Placement = pos=(25.62,21.1,0) rot=(0,0,1;0rad)
FEATURE [App::Link] R9_R_0603_1608Metric_fe9d9f34c5f9_ln_009  label="R28_R_0603_1608Metric_db2da8ac741f"
  LinkPlacement = pos=(13.3,84.0715,0) rot=(0,0,1;1.5708rad)
  LinkedObject = -> Shape002
  Placement = pos=(13.3,84.0715,0) rot=(0,0,1;1.5708rad)
FEATURE [App::Link] C38_C_0805_2012Metric_74cbd35bff10_ln_005  label="C25_C_0805_2012Metric_d4570dd2b406"
  LinkPlacement = pos=(21.9,8.7,0) rot=(0,0,1;3.14159rad)
  LinkedObject = -> Shape005
  Placement = pos=(21.9,8.7,0) rot=(0,0,1;3.14159rad)
FEATURE [Part::Feature] Shape011  label="L5_L_0603_1608Metric_90973c27a168"
  Placement = pos=(5.1,81.1115,0) rot=(0,0,1;1.5708rad)
  shape: bbox 0.8 x 1.6 x 0.8 mm, 28 faces (baked)
FEATURE [App::Link] R21_R_0805_2012Metric_4eff570911b6_ln_004  label="R26_R_0805_2012Metric_215f856b24f5"
  LinkPlacement = pos=(34.3,13.9,0) rot=(0,0,1;0rad)
  LinkedObject = -> Shape007
  Placement = pos=(34.3,13.9,0) rot=(0,0,1;0rad)
FEATURE [App::Link] L5_L_0603_1608Metric_90973c27a168_ln_  label="L6_L_0603_1608Metric_227bb48d5cae"
  LinkPlacement = pos=(5.1,60.4265,0) rot=(0,0,1;1.5708rad)
  LinkedObject = -> Shape011
  Placement = pos=(5.1,60.4265,0) rot=(0,0,1;1.5708rad)
FEATURE [App::Link] C15_C_0603_1608Metric_09ddd0478757_ln_010  label="C14_C_0603_1608Metric_a25fa12fbfe8"
  LinkPlacement = pos=(11.3,24.6,0) rot=(0,0,-1;1.5708rad)
  LinkedObject = -> Shape003
  Placement = pos=(11.3,24.6,0) rot=(0,0,-1;1.5708rad)
FEATURE [App::Link] R9_R_0603_1608Metric_fe9d9f34c5f9_ln_010  label="R31_R_0603_1608Metric_1647f0dc400e"
  LinkPlacement = pos=(18.7,68.3115,0) rot=(0,0,1;1.5708rad)
  LinkedObject = -> Shape002
  Placement = pos=(18.7,68.3115,0) rot=(0,0,1;1.5708rad)
FEATURE [App::Link] C38_C_0805_2012Metric_74cbd35bff10_ln_006  label="C37_C_0805_2012Metric_821d07cd279f"
  LinkPlacement = pos=(7.5,57.7115,0) rot=(0,0,1;3.14159rad)
  LinkedObject = -> Shape005
  Placement = pos=(7.5,57.7115,0) rot=(0,0,1;3.14159rad)
FEATURE [App::Link] C5_C_2220_5750Metric_40789e461117_ln_001  label="C4_C_2220_5750Metric_aeb9c5b40f04"
  LinkPlacement = pos=(65.498,23.622,0) rot=(0,0,-1;1.5708rad)
  LinkedObject = -> Shape010
  Placement = pos=(65.498,23.622,0) rot=(0,0,-1;1.5708rad)
FEATURE [Part::Feature] Part__Feature002  label="CAS_c_D2B"
  Placement = pos=(0,-2.4,-3e-16) rot=(0,0,1;0rad)
  shape: bbox 5.4 x 2.5 x 5.6 mm, 110 faces (baked)
FEATURE [Part::Feature] Part__Feature003  label="Dual_s"
  Placement = pos=(0.3,-0.6,0.64) rot=(0,0,1;0rad)
  shape: bbox 0.6 x 0.6 x 0.7 mm, 14 faces (baked)
FEATURE [Part::Feature] Part__Feature004  label="Dual_s001"
  Placement = pos=(0.3,-0.6,-0.64) rot=(0,0,1;0rad)
  shape: bbox 0.6 x 0.6 x 0.7 mm, 14 faces (baked)
FEATURE [App::Part] CAS_D20B1  label="SW5_CAS-D20B1_b4c165cab9b4[2]"
  Group = -> [Part__Feature002,Part__Feature003,Part__Feature004]
  Origin = -> Origin009
  Placement = pos=(4.29,22.754,2.5) rot=(0,0.707107,0.707107;3.14159rad)
FEATURE [App::Link] R9_R_0603_1608Metric_fe9d9f34c5f9_ln_011  label="R35_R_0603_1608Metric_3c432ada0ca8"
  LinkPlacement = pos=(22.7,72.9115,0) rot=(0,0,1;1.5708rad)
  LinkedObject = -> Shape002
  Placement = pos=(22.7,72.9115,0) rot=(0,0,1;1.5708rad)
FEATURE [App::Link] U7_SOT_23_ed8fd63cd947_ln_  label="U8_SOT_23_df60fcb6f98c"
  LinkPlacement = pos=(25.3625,13.6,0) rot=(0,0,1;3.14159rad)
  LinkedObject = -> Shape009
  Placement = pos=(25.3625,13.6,0) rot=(0,0,1;3.14159rad)
FEATURE [App::Link] L5_L_0603_1608Metric_90973c27a168_ln_001  label="L4_L_0603_1608Metric_8fa15f76ae30"
  LinkPlacement = pos=(5.1,70.5865,0) rot=(0,0,1;1.5708rad)
  LinkedObject = -> Shape011
  Placement = pos=(5.1,70.5865,0) rot=(0,0,1;1.5708rad)
FEATURE [App::Link] SW1_CAS_120B1_eba1f44a47b7_2__ln_  label="SW3_CAS-120B1_d768a4589788[2]"
  LinkPlacement = pos=(29.21,62.484,2.5) rot=(0.57735,-0.57735,-0.57735;2.0944rad)
  LinkedObject = -> CAS_120B1
  Placement = pos=(29.21,62.484,2.5) rot=(0.57735,-0.57735,-0.57735;2.0944rad)
FEATURE [App::Link] C15_C_0603_1608Metric_09ddd0478757_ln_011  label="C32_C_0603_1608Metric_89b2b6ef811b"
  LinkPlacement = pos=(9.3,70.7115,0) rot=(0,0,1;1.5708rad)
  LinkedObject = -> Shape003
  Placement = pos=(9.3,70.7115,0) rot=(0,0,1;1.5708rad)
FEATURE [App::Link] C38_C_0805_2012Metric_74cbd35bff10_ln_007  label="C36_C_0805_2012Metric_4e65c6641553"
  LinkPlacement = pos=(7.9,78.1115,0) rot=(0,0,1;3.14159rad)
  LinkedObject = -> Shape005
  Placement = pos=(7.9,78.1115,0) rot=(0,0,1;3.14159rad)
FEATURE [App::Link] C5_C_2220_5750Metric_40789e461117_ln_002  label="C2_C_2220_5750Metric_dfcbf9cf85c4"
  LinkPlacement = pos=(53.498,23.622,0) rot=(0,0,-1;1.5708rad)
  LinkedObject = -> Shape010
  Placement = pos=(53.498,23.622,0) rot=(0,0,-1;1.5708rad)
FEATURE [App::Link] C15_C_0603_1608Metric_09ddd0478757_ln_012  label="C23_C_0603_1608Metric_094c659e187e"
  LinkPlacement = pos=(25.65,25.3,0) rot=(0,0,1;3.14159rad)
  LinkedObject = -> Shape003
  Placement = pos=(25.65,25.3,0) rot=(0,0,1;3.14159rad)
FEATURE [App::Link] R21_R_0805_2012Metric_4eff570911b6_ln_005  label="R20_R_0805_2012Metric_ea78c8c8eecd"
  LinkPlacement = pos=(34.3,30.2,0) rot=(0,0,1;0rad)
  LinkedObject = -> Shape007
  Placement = pos=(34.3,30.2,0) rot=(0,0,1;0rad)
FEATURE [App::Link] C38_C_0805_2012Metric_74cbd35bff10_ln_008  label="C16_C_0805_2012Metric_e5af641f3413"
  LinkPlacement = pos=(12.5,33.7,0) rot=(0,0,1;0rad)
  LinkedObject = -> Shape005
  Placement = pos=(12.5,33.7,0) rot=(0,0,1;0rad)
FEATURE [App::Link] R9_R_0603_1608Metric_fe9d9f34c5f9_ln_012  label="R34_R_0603_1608Metric_211ac095cb09"
  LinkPlacement = pos=(22.7,63.1115,0) rot=(0,0,1;1.5708rad)
  LinkedObject = -> Shape002
  Placement = pos=(22.7,63.1115,0) rot=(0,0,1;1.5708rad)
FEATURE [App::Link] C15_C_0603_1608Metric_09ddd0478757_ln_013  label="C27_C_0603_1608Metric_298082643862"
  LinkPlacement = pos=(23.6375,16.1,0) rot=(0,0,1;3.14159rad)
  LinkedObject = -> Shape003
  Placement = pos=(23.6375,16.1,0) rot=(0,0,1;3.14159rad)
FEATURE [App::Link] R21_R_0805_2012Metric_4eff570911b6_ln_006  label="R2_R_0805_2012Metric_96e20fc01cb7"
  LinkPlacement = pos=(44.564,33.296,0) rot=(0,0,1;1.5708rad)
  LinkedObject = -> Shape007
  Placement = pos=(44.564,33.296,0) rot=(0,0,1;1.5708rad)
FEATURE [App::Link] R9_R_0603_1608Metric_fe9d9f34c5f9_ln_013  label="R13_R_0603_1608Metric_df329fa1d19c"
  LinkPlacement = pos=(29.7,36.5,0) rot=(0,0,-1;1.5708rad)
  LinkedObject = -> Shape002
  Placement = pos=(29.7,36.5,0) rot=(0,0,-1;1.5708rad)
FEATURE [App::Link] U3_SOT_23_5_e32904241429_ln_  label="U2_SOT_23_5_6f2eb00efaad"
  LinkPlacement = pos=(34.37,72.8615,0) rot=(0,0,1;0rad)
  LinkedObject = -> Shape008
  Placement = pos=(34.37,72.8615,0) rot=(0,0,1;0rad)
FEATURE [App::Link] L5_L_0603_1608Metric_90973c27a168_ln_002  label="L2_L_0603_1608Metric_6584b5c4d191"
  LinkPlacement = pos=(9.3,33.1,0) rot=(0,0,-1;1.5708rad)
  LinkedObject = -> Shape011
  Placement = pos=(9.3,33.1,0) rot=(0,0,-1;1.5708rad)
FEATURE [App::Link] L5_L_0603_1608Metric_90973c27a168_ln_003  label="L3_L_0603_1608Metric_80e3bdf1ad67"
  LinkPlacement = pos=(9.3,8.7,0) rot=(0,0,1;1.5708rad)
  LinkedObject = -> Shape011
  Placement = pos=(9.3,8.7,0) rot=(0,0,1;1.5708rad)
FEATURE [App::Link] R21_R_0805_2012Metric_4eff570911b6_ln_007  label="R23_R_0805_2012Metric_772e2aabec3d"
  LinkPlacement = pos=(34.3,19.85,0) rot=(0,0,1;0rad)
  LinkedObject = -> Shape007
  Placement = pos=(34.3,19.85,0) rot=(0,0,1;0rad)
FEATURE [App::Link] C38_C_0805_2012Metric_74cbd35bff10_ln_009  label="C17_C_0805_2012Metric_9d67934c64c5"
  LinkPlacement = pos=(12.1,8.1,0) rot=(0,0,1;0rad)
  LinkedObject = -> Shape005
  Placement = pos=(12.1,8.1,0) rot=(0,0,1;0rad)
FEATURE [App::Link] U10_SOT_23_6_8cf1dc40b667_ln_001  label="U9_SOT_23_6_77935cb89beb"
  LinkPlacement = pos=(21.85,78.4715,0) rot=(0,0,1;3.14159rad)
  LinkedObject = -> Shape006
  Placement = pos=(21.85,78.4715,0) rot=(0,0,1;3.14159rad)
FEATURE [App::Link] C38_C_0805_2012Metric_74cbd35bff10_ln_010  label="C19_C_0805_2012Metric_f233b5c27be5"
  LinkPlacement = pos=(21.9,33.1,0) rot=(0,0,1;3.14159rad)
  LinkedObject = -> Shape005
  Placement = pos=(21.9,33.1,0) rot=(0,0,1;3.14159rad)
FEATURE [App::Link] SW1_CAS_120B1_eba1f44a47b7_2__ln_001  label="SW2_CAS-120B1_de4e8c04cc20[2]"
  LinkPlacement = pos=(29.242,72.898,2.5) rot=(0.57735,-0.57735,-0.57735;2.0944rad)
  LinkedObject = -> CAS_120B1
  Placement = pos=(29.242,72.898,2.5) rot=(0.57735,-0.57735,-0.57735;2.0944rad)
FEATURE [App::Link] R21_R_0805_2012Metric_4eff570911b6_ln_008  label="R25_R_0805_2012Metric_61226d1b2b79"
  LinkPlacement = pos=(34.3,15.9,0) rot=(0,0,1;0rad)
  LinkedObject = -> Shape007
  Placement = pos=(34.3,15.9,0) rot=(0,0,1;0rad)
FEATURE [App::Link] C15_C_0603_1608Metric_09ddd0478757_ln_014  label="C8_C_0603_1608Metric_fd007361b396"
  LinkPlacement = pos=(36.322,65.278,0) rot=(0,0,1;0rad)
  LinkedObject = -> Shape003
  Placement = pos=(36.322,65.278,0) rot=(0,0,1;0rad)
FEATURE [App::Link] C15_C_0603_1608Metric_09ddd0478757_ln_015  label="C7_C_0603_1608Metric_2aaeb20b4386"
  LinkPlacement = pos=(36.4755,75.438,0) rot=(0,0,1;0rad)
  LinkedObject = -> Shape003
  Placement = pos=(36.4755,75.438,0) rot=(0,0,1;0rad)
FEATURE [App::Link] C15_C_0603_1608Metric_09ddd0478757_ln_016  label="C26_C_0603_1608Metric_365ecaa62ea9"
  LinkPlacement = pos=(23.7,38.95,0) rot=(0,0,1;3.14159rad)
  LinkedObject = -> Shape003
  Placement = pos=(23.7,38.95,0) rot=(0,0,1;3.14159rad)
FEATURE [App::Link] C15_C_0603_1608Metric_09ddd0478757_ln_017  label="C11_C_0603_1608Metric_54b4a60d9175"
  LinkPlacement = pos=(10.2875,21.3,0) rot=(0,0,1;3.14159rad)
  LinkedObject = -> Shape003
  Placement = pos=(10.2875,21.3,0) rot=(0,0,1;3.14159rad)
FEATURE [App::Link] R21_R_0805_2012Metric_4eff570911b6_ln_009  label="R24_R_0805_2012Metric_5be639e06338"
  LinkPlacement = pos=(34.3,17.9,0) rot=(0,0,1;0rad)
  LinkedObject = -> Shape007
  Placement = pos=(34.3,17.9,0) rot=(0,0,1;0rad)
FEATURE [App::Link] SW5_CAS_D20B1_b4c165cab9b4_2__ln_  label="SW4_CAS-D20B1_eed64a9be6db[2]"
  LinkPlacement = pos=(4.29,15.168,2.5) rot=(0,0.707107,0.707107;3.14159rad)
  LinkedObject = -> CAS_D20B1
  Placement = pos=(4.29,15.168,2.5) rot=(0,0.707107,0.707107;3.14159rad)
FEATURE [App::Link] R9_R_0603_1608Metric_fe9d9f34c5f9_ln_014  label="R17_R_0603_1608Metric_026225098221"
  LinkPlacement = pos=(28.1,13.3,0) rot=(0,0,1;1.5708rad)
  LinkedObject = -> Shape002
  Placement = pos=(28.1,13.3,0) rot=(0,0,1;1.5708rad)
FEATURE [App::Link] D3_LED_0603_1608Metric_70bb5031e2ff_ln_002  label="D4_LED_0603_1608Metric_dc75b572683f"
  LinkPlacement = pos=(4.7,28.175,0) rot=(0,0,-1;1.5708rad)
  LinkedObject = -> Shape004
  Placement = pos=(4.7,28.175,0) rot=(0,0,-1;1.5708rad)
FEATURE [App::Link] C15_C_0603_1608Metric_09ddd0478757_ln_018  label="C44_C_0603_1608Metric_1898ed5e7091"
  LinkPlacement = pos=(36.9,33.02,0) rot=(0,0,1;1.5708rad)
  LinkedObject = -> Shape003
  Placement = pos=(36.9,33.02,0) rot=(0,0,1;1.5708rad)
FEATURE [App::Link] R21_R_0805_2012Metric_4eff570911b6_ln_010  label="R22_R_0805_2012Metric_455d99f14320"
  LinkPlacement = pos=(34.3,26.2,0) rot=(0,0,1;0rad)
  LinkedObject = -> Shape007
  Placement = pos=(34.3,26.2,0) rot=(0,0,1;0rad)
FEATURE [App::Link] R9_R_0603_1608Metric_fe9d9f34c5f9_ln_015  label="R18_R_0603_1608Metric_e5275256b3fe"
  LinkPlacement = pos=(22.7,13.246,0) rot=(0,0,-1;1.5708rad)
  LinkedObject = -> Shape002
  Placement = pos=(22.7,13.246,0) rot=(0,0,-1;1.5708rad)
FEATURE [App::Link] U3_SOT_23_5_e32904241429_ln_001  label="U1_SOT_23_5_8fc5e1a9f18e"
  LinkPlacement = pos=(34.37,83.0215,0) rot=(0,0,1;0rad)
  LinkedObject = -> Shape008
  Placement = pos=(34.37,83.0215,0) rot=(0,0,1;0rad)
FEATURE [App::Part] Top_ed05
  Group = -> [Shape,Shape001,Shape002,D6_D_SOD_123_86f777a7cf57_ln_,Shape003,C15_C_0603_1608Metric_09ddd0478757_ln_,Shape004,Shape005,R9_R_0603_1608Metric_fe9d9f34c5f9_ln_,C15_C_0603_1608Metric_09ddd0478757_ln_001,CAS_120B1,R9_R_0603_1608Metric_fe9d9f34c5f9_ln_001,R9_R_0603_1608Metric_fe9d9f34c5f9_ln_002,C15_C_0603_1608Metric_09ddd0478757_ln_002,C38_C_0805_2012Metric_74cbd35bff10_ln_,Shape006,+74 more]
  Origin = -> Origin003
FEATURE [Part::Feature] Shape012  label="R36_R_Axial_DIN0617_L170mm_D60mm_P3048mm_Horizontal_e9082eb0809f"
  Placement = pos=(80.8,75.438,-1.6) rot=(0.707107,-0.707107,0;3.14159rad)
  shape: bbox 6.494 x 31.54 x 9.247 mm, 17 faces (baked)
FEATURE [App::Link] C38_C_0805_2012Metric_74cbd35bff10_ln_011  label="C30_C_0805_2012Metric_99b0a26469c9"
  LinkPlacement = pos=(25.8,20.7,-1.6) rot=(1,0,0;3.14159rad)
  LinkedObject = -> Shape005
  Placement = pos=(25.8,20.7,-1.6) rot=(1,0,0;3.14159rad)
FEATURE [App::Link] C15_C_0603_1608Metric_09ddd0478757_ln_019  label="C10_C_0603_1608Metric_a9055c7e1f35"
  LinkPlacement = pos=(10,27.2,-1.6) rot=(0,1,0;3.14159rad)
  LinkedObject = -> Shape003
  Placement = pos=(10,27.2,-1.6) rot=(0,1,0;3.14159rad)
FEATURE [App::Link] C38_C_0805_2012Metric_74cbd35bff10_ln_012  label="C12_C_0805_2012Metric_7a36f4b334d7"
  LinkPlacement = pos=(4.7,23.5,-1.6) rot=(0.707107,0.707107,0;3.14159rad)
  LinkedObject = -> Shape005
  Placement = pos=(4.7,23.5,-1.6) rot=(0.707107,0.707107,0;3.14159rad)
FEATURE [Part::Feature] Shape013  label="J4_Broadcom_AFBR-16xxZ_Horizontal_9b6c4e7f7e3c"
  Placement = pos=(11.2,84.664,-1.6) rot=(0,1,0;3.14159rad)
  shape: bbox 17.71 x 11.7 x 11.4 mm, 100 faces (baked)
FEATURE [App::Link] R21_R_0805_2012Metric_4eff570911b6_ln_011  label="R11_R_0805_2012Metric_904fb74af206"
  LinkPlacement = pos=(23.492,38.646,-1.6) rot=(1,0,0;3.14159rad)
  LinkedObject = -> Shape007
  Placement = pos=(23.492,38.646,-1.6) rot=(1,0,0;3.14159rad)
FEATURE [Part::Feature] Part__Feature005  label="79fa9e9c-a09d-11ed-8f45-a0cec80452fd_part"
  shape: bbox 8.4 x 14.4 x 13.5 mm, 26 faces (baked)
FEATURE [App::Part] _9fa9e9c_a09d_11ed_8f45_a0cec80452fd  label="79fa9e9c-a09d-11ed-8f45-a0cec80452fd"
  Group = -> [Part__Feature005]
  Origin = -> Origin010
FEATURE [Part::Feature] Part__Feature006  label="79faa16c-a09d-11ed-8f45-a0cec80452fd_part"
  shape: bbox 1.1 x 1.1 x 2.6 mm, 12 faces (baked)
FEATURE [Part::Feature] Part__Feature007  label="79faa16c-a09d-11ed-8f45-a0cec80452fd_part001"
  shape: bbox 1.1 x 1.1 x 2.6 mm, 12 faces (baked)
FEATURE [Part::Feature] Part__Feature008  label="79faa16c-a09d-11ed-8f45-a0cec80452fd_part002"
  shape: bbox 1.1 x 1.1 x 2.6 mm, 12 faces (baked)
FEATURE [Part::Feature] Part__Feature009  label="79faa16c-a09d-11ed-8f45-a0cec80452fd_part003"
  shape: bbox 1.1 x 1.1 x 2.6 mm, 12 faces (baked)
FEATURE [App::Part] _9faa16c_a09d_11ed_8f45_a0cec80452fd_part  label="79faa16c-a09d-11ed-8f45-a0cec80452fd_part004"
  Group = -> [Part__Feature006,Part__Feature007,Part__Feature008,Part__Feature009]
  Origin = -> Origin011
FEATURE [App::Part] _9faa16c_a09d_11ed_8f45_a0cec80452fd  label="79faa16c-a09d-11ed-8f45-a0cec80452fd"
  Group = -> [_9faa16c_a09d_11ed_8f45_a0cec80452fd_part]
  Origin = -> Origin012
FEATURE [App::Part] _9fa99c4_a09d_11ed_8f45_a0cec80452fd  label="79fa99c4-a09d-11ed-8f45-a0cec80452fd"
  Group = -> [_9fa9e9c_a09d_11ed_8f45_a0cec80452fd,_9faa16c_a09d_11ed_8f45_a0cec80452fd]
  Origin = -> Origin013
FEATURE [App::Part] CQ_assembly  label="J1_CQ assembly_c40872800de1"
  Group = -> [_9fa99c4_a09d_11ed_8f45_a0cec80452fd]
  Origin = -> Origin014
  Placement = pos=(12.4,40.678,-1.6) rot=(0.707107,0.707107,0;3.14159rad)
FEATURE [Part::Feature] Shape014  label="J10_PinHeader_1x02_P254mm_Horizontal_7643f22ec726"
  Placement = pos=(24.8,74.1115,-1.6) rot=(0,1,0;3.14159rad)
  shape: bbox 10.36 x 5.08 x 5.54 mm, 58 faces (baked)
FEATURE [App::Link] C38_C_0805_2012Metric_74cbd35bff10_ln_013  label="C28_C_0805_2012Metric_76606bb4505c"
  LinkPlacement = pos=(25.8,28.232,-1.6) rot=(1,0,0;3.14159rad)
  LinkedObject = -> Shape005
  Placement = pos=(25.8,28.232,-1.6) rot=(1,0,0;3.14159rad)
FEATURE [Part::Feature] Shape015  label="J2_C-413638-E_37cd69765024[2]"
  Placement = pos=(110.98,49.92,-5.6) rot=(0.57735,-0.57735,0.57735;4.18879rad)
  shape: bbox 25.2 x 94 x 14.8 mm, 484 faces (baked)
FEATURE [App::Link] R9_R_0603_1608Metric_fe9d9f34c5f9_ln_016  label="R4_R_0603_1608Metric_d5e5e0a8c182"
  LinkPlacement = pos=(3.875,35.5,-1.6) rot=(0.707107,-0.707107,0;3.14159rad)
  LinkedObject = -> Shape002
  Placement = pos=(3.875,35.5,-1.6) rot=(0.707107,-0.707107,0;3.14159rad)
FEATURE [App::Link] R9_R_0603_1608Metric_fe9d9f34c5f9_ln_017  label="R1_R_0603_1608Metric_12d23797164c"
  LinkPlacement = pos=(4.1,9.525,-1.6) rot=(0.707107,0.707107,0;3.14159rad)
  LinkedObject = -> Shape002
  Placement = pos=(4.1,9.525,-1.6) rot=(0.707107,0.707107,0;3.14159rad)
FEATURE [App::Link] J10_PinHeader_1x02_P254mm_Horizontal_7643f22ec726_ln_  label="J11_PinHeader_1x02_P254mm_Horizontal_fc1500a1b926"
  LinkPlacement = pos=(24.8,63.9515,-1.6) rot=(0,1,0;3.14159rad)
  LinkedObject = -> Shape014
  Placement = pos=(24.8,63.9515,-1.6) rot=(0,1,0;3.14159rad)
FEATURE [Part::Feature] Shape016  label="J13_1_cfcac89c0bd5[2]"
  Placement = pos=(96.5,44.12,-1.6) rot=(0.707107,-0.707107,0;3.14159rad)
  shape: bbox 7 x 4.98 x 4.98 mm, 13 faces (baked)
FEATURE [Part::Feature] Shape017  label="R39_R_4020_10251Metric_6d765f65bd79"
  Placement = pos=(64.4,75.4,-1.6) rot=(1,0,0;3.14159rad)
  shape: bbox 10.2 x 5.1 x 0.6 mm, 26 faces (baked)
FEATURE [Part::Feature] Part__Feature010  label="T1T1M-02-T-SH-L"
  Placement = pos=(0,0,0) rot=(1,0,0;1.5708rad)
  shape: bbox 4.4 x 4.6 x 5.2 mm, 86 faces (baked)
FEATURE [Part::Feature] Part__Feature011  label="P2T1M-02-F-SH-L"
  Placement = pos=(0,0,0) rot=(1,0,0;1.5708rad)
  shape: bbox 1.2 x 2.22 x 1.2 mm, 19 faces (baked)
FEATURE [Part::Feature] Part__Feature012  label="P22T1M-02-F-SH-L"
  Placement = pos=(0,0,0) rot=(1,0,0;1.5708rad)
  shape: bbox 1.2 x 0.4 x 3.971 mm, 15 faces (baked)
FEATURE [App::Part] T1M_02_F_SH_L  label="J6_T1M-02-F-SH-L_0a7fe3b67a9c[2]"
  Group = -> [Part__Feature010,Part__Feature011,Part__Feature012]
  Origin = -> Origin015
  Placement = pos=(31.4,67.734,-3.98) rot=(0.57735,0.57735,-0.57735;4.18879rad)
FEATURE [Part::Feature] Shape018  label="HS1_sk687_9ae714bd8fdf[2]"
  Placement = pos=(33.982,3.642,-1.55) rot=(0,0.707107,-0.707107;3.14159rad)
  shape: bbox 42 x 50 x 35 mm, 258 faces (baked)
FEATURE [App::Link] J6_T1M_02_F_SH_L_0a7fe3b67a9c_2__ln_  label="J7_T1M-02-F-SH-L_7059b7eb8092[2]"
  LinkPlacement = pos=(31.4,77.894,-3.98) rot=(0.57735,0.57735,-0.57735;4.18879rad)
  LinkedObject = -> T1M_02_F_SH_L
  Placement = pos=(31.4,77.894,-3.98) rot=(0.57735,0.57735,-0.57735;4.18879rad)
FEATURE [App::Link] R39_R_4020_10251Metric_6d765f65bd79_ln_  label="R38_R_4020_10251Metric_23694b22d5d4"
  LinkPlacement = pos=(64.4,81.2,-1.6) rot=(1,0,0;3.14159rad)
  LinkedObject = -> Shape017
  Placement = pos=(64.4,81.2,-1.6) rot=(1,0,0;3.14159rad)
FEATURE [App::Link] C38_C_0805_2012Metric_74cbd35bff10_ln_014  label="C13_C_0805_2012Metric_5e4ca477a655"
  LinkPlacement = pos=(9.9,21.7,-1.6) rot=(1,0,0;3.14159rad)
  LinkedObject = -> Shape005
  Placement = pos=(9.9,21.7,-1.6) rot=(1,0,0;3.14159rad)
FEATURE [App::Link] J10_PinHeader_1x02_P254mm_Horizontal_7643f22ec726_ln_001  label="J9_PinHeader_1x02_P254mm_Horizontal_9237b5c6f450"
  LinkPlacement = pos=(24.8,84.2715,-1.6) rot=(0,1,0;3.14159rad)
  LinkedObject = -> Shape014
  Placement = pos=(24.8,84.2715,-1.6) rot=(0,1,0;3.14159rad)
FEATURE [App::Link] R9_R_0603_1608Metric_fe9d9f34c5f9_ln_018  label="R5_R_0603_1608Metric_697492a11508"
  LinkPlacement = pos=(3.875,31.775,-1.6) rot=(0.707107,-0.707107,0;3.14159rad)
  LinkedObject = -> Shape002
  Placement = pos=(3.875,31.775,-1.6) rot=(0.707107,-0.707107,0;3.14159rad)
FEATURE [App::Link] J4_Broadcom_AFBR_16xxZ_Horizontal_9b6c4e7f7e3c_ln_  label="J5_Broadcom_AFBR-16xxZ_Horizontal_cc90251d43e9"
  LinkPlacement = pos=(11.2,64.344,-1.6) rot=(0,1,0;3.14159rad)
  LinkedObject = -> Shape013
  Placement = pos=(11.2,64.344,-1.6) rot=(0,1,0;3.14159rad)
FEATURE [App::Link] C15_C_0603_1608Metric_09ddd0478757_ln_020  label="C9_C_0603_1608Metric_8758c5b1e71b"
  LinkPlacement = pos=(10,28.7,-1.6) rot=(0,1,0;3.14159rad)
  LinkedObject = -> Shape003
  Placement = pos=(10,28.7,-1.6) rot=(0,1,0;3.14159rad)
FEATURE [App::Link] R9_R_0603_1608Metric_fe9d9f34c5f9_ln_019  label="R7_R_0603_1608Metric_6e0015b41d89"
  LinkPlacement = pos=(2.9,24.5,-1.6) rot=(0.707107,-0.707107,0;3.14159rad)
  LinkedObject = -> Shape002
  Placement = pos=(2.9,24.5,-1.6) rot=(0.707107,-0.707107,0;3.14159rad)
FEATURE [Part::Feature] Part__Feature013  label="CFP_RB4_42X40X20_L43H41T21S37.5S110.2LL4F1.25"
  shape: bbox 43 x 45 x 21 mm, 30 faces (baked)
FEATURE [Part::Feature] Part__Feature014  label="CFP_RB4_42X40X20_L43H41T21S37.5S110.2LL4F1.026"
  shape: bbox 8.475 x 4.477 x 0.005 mm, 19 faces (baked)
FEATURE [Part::Feature] Part__Feature015  label="CFP_RB4_42X40X20_L43H41T21S37.5S110.2LL4F1.027"
  shape: bbox 10.33 x 4.477 x 0.005 mm, 25 faces (baked)
FEATURE [Part::Feature] Part__Feature016  label="CFP_RB4_42X40X20_L43H41T21S37.5S110.2LL4F1.028"
  shape: bbox 5.39 x 4.477 x 0.005 mm, 13 faces (baked)
FEATURE [App::Part] CFP_RB4_42X40X20_L43H41T21S37_5S110_2LL4F1_25  label="C1_CFP_RB4_42X40X20_L43H41T21S37.5S110.2LL4F1.029_59f146c23d11[2]"
  Group = -> [Part__Feature013,Part__Feature014,Part__Feature015,Part__Feature016]
  Origin = -> Origin016
  Placement = pos=(56.028,56.336,-1.6) rot=(0.57735,-0.57735,0.57735;4.18879rad)
FEATURE [Part::Feature] Shape019  label="Q1_TO-247-4_Vertical_4070ae466a86"
  Placement = pos=(40.55,42.209,-1.6) rot=(0.707107,-0.707107,0;3.14159rad)
  shape: bbox 5.03 x 15.9 x 41.1 mm, 74 faces (baked)
FEATURE [App::Link] J13_1_cfcac89c0bd5_2__ln_  label="J14_1_45c35c22a121[2]"
  LinkPlacement = pos=(96.5,64.44,-1.6) rot=(0.707107,-0.707107,0;3.14159rad)
  LinkedObject = -> Shape016
  Placement = pos=(96.5,64.44,-1.6) rot=(0.707107,-0.707107,0;3.14159rad)
FEATURE [Part::Feature] Part__Feature017  label="RKZ-xx2005D_case"
  shape: bbox 19.65 x 10.2 x 7.05 mm, 112 faces (baked)
FEATURE [Part::Feature] Part__Feature018  label="RKZ-xx2005D_pin1(+Vin)"
  shape: bbox 0.5 x 4.6 x 0.25 mm, 6 faces (baked)
FEATURE [Part::Feature] Part__Feature019  label="RKZ-xx2005D_pin7(+Vout)"
  shape: bbox 0.5 x 4.6 x 0.25 mm, 6 faces (baked)
FEATURE [Part::Feature] Part__Feature020  label="RKZ-xx2005D_pin5(-Vout)"
  shape: bbox 0.5 x 4.6 x 0.25 mm, 6 faces (baked)
FEATURE [Part::Feature] Part__Feature021  label="RKZ-xx2005D_pin6(Com)"
  shape: bbox 0.5 x 4.6 x 0.25 mm, 6 faces (baked)
FEATURE [Part::Feature] Part__Feature022  label="RKZ-xx2005D_pin2(-Vin)"
  shape: bbox 0.5 x 4.6 x 0.25 mm, 6 faces (baked)
FEATURE [Part::Feature] Part__Feature023  label="RKZ-xx2005D_potting"
  shape: bbox 18.55 x 8.95 x 6 mm, 6 faces (baked)
FEATURE [App::Part] RKZ_xx2005D  label="U6_RKZ_xx2005D_0645041a10aa[2]"
  Group = -> [Part__Feature017,Part__Feature018,Part__Feature019,Part__Feature020,Part__Feature021,Part__Feature022,Part__Feature023]
  Origin = -> Origin017
  Placement = pos=(18.85,12.664,-1.6) rot=(-1,0,0;1.5708rad)
FEATURE [App::Link] U6_RKZ_xx2005D_0645041a10aa_2__ln_  label="U4_RKZ_xx2005D_740929d25b34[2]"
  LinkPlacement = pos=(18.85,33.276,-1.6) rot=(-1,0,0;1.5708rad)
  LinkedObject = -> RKZ_xx2005D
  Placement = pos=(18.85,33.276,-1.6) rot=(-1,0,0;1.5708rad)
FEATURE [App::Link] J6_T1M_02_F_SH_L_0a7fe3b67a9c_2__ln_001  label="J8_T1M-02-F-SH-L_f87a2e85d4db[2]"
  LinkPlacement = pos=(31.4,57.574,-3.98) rot=(0.57735,0.57735,-0.57735;4.18879rad)
  LinkedObject = -> T1M_02_F_SH_L
  Placement = pos=(31.4,57.574,-3.98) rot=(0.57735,0.57735,-0.57735;4.18879rad)
FEATURE [App::Link] Q1_TO_247_4_Vertical_4070ae466a86_ln_  label="Q2_TO-247-4_Vertical_c7c841d41241"
  LinkPlacement = pos=(40.55,25.209,-1.6) rot=(0.707107,-0.707107,0;3.14159rad)
  LinkedObject = -> Shape019
  Placement = pos=(40.55,25.209,-1.6) rot=(0.707107,-0.707107,0;3.14159rad)
FEATURE [App::Link] C38_C_0805_2012Metric_74cbd35bff10_ln_015  label="C29_C_0805_2012Metric_ea01a7009c54"
  LinkPlacement = pos=(25.7995,25.692,-1.6) rot=(0,1,0;3.14159rad)
  LinkedObject = -> Shape005
  Placement = pos=(25.7995,25.692,-1.6) rot=(0,1,0;3.14159rad)
FEATURE [App::Link] L5_L_0603_1608Metric_90973c27a168_ln_004  label="L1_L_0603_1608Metric_e9d47b7cc21e"
  LinkPlacement = pos=(7.375,23.5,-1.6) rot=(1,0,0;3.14159rad)
  LinkedObject = -> Shape011
  Placement = pos=(7.375,23.5,-1.6) rot=(1,0,0;3.14159rad)
FEATURE [App::Link] R21_R_0805_2012Metric_4eff570911b6_ln_012  label="R12_R_0805_2012Metric_000eced81897"
  LinkPlacement = pos=(24.892,7.874,-1.6) rot=(1,0,0;3.14159rad)
  LinkedObject = -> Shape007
  Placement = pos=(24.892,7.874,-1.6) rot=(1,0,0;3.14159rad)
FEATURE [App::Link] R9_R_0603_1608Metric_fe9d9f34c5f9_ln_020  label="R6_R_0603_1608Metric_4e81408e4251"
  LinkPlacement = pos=(3.9,28.175,-1.6) rot=(0.707107,-0.707107,0;3.14159rad)
  LinkedObject = -> Shape002
  Placement = pos=(3.9,28.175,-1.6) rot=(0.707107,-0.707107,0;3.14159rad)
FEATURE [App::Link] R36_R_Axial_DIN0617_L170mm_D60mm_P3048mm_Horizontal_e9082eb0809f_ln_  label="R37_R_Axial_DIN0617_L170mm_D60mm_P3048mm_Horizontal_4fcf1ba42225"
  LinkPlacement = pos=(80.8,41.91,-1.6) rot=(0.707107,-0.707107,0;3.14159rad)
  LinkedObject = -> Shape012
  Placement = pos=(80.8,41.91,-1.6) rot=(0.707107,-0.707107,0;3.14159rad)
FEATURE [App::Link] J13_1_cfcac89c0bd5_2__ln_001  label="J12_1_5d39db0f3e7c[2]"
  LinkPlacement = pos=(96.5,23.8,-1.6) rot=(0.707107,-0.707107,0;3.14159rad)
  LinkedObject = -> Shape016
  Placement = pos=(96.5,23.8,-1.6) rot=(0.707107,-0.707107,0;3.14159rad)
FEATURE [App::Link] J13_1_cfcac89c0bd5_2__ln_002  label="J15_1_77f750f6aa21[2]"
  LinkPlacement = pos=(96.5,84.76,-1.6) rot=(0.707107,-0.707107,0;3.14159rad)
  LinkedObject = -> Shape016
  Placement = pos=(96.5,84.76,-1.6) rot=(0.707107,-0.707107,0;3.14159rad)
FEATURE [App::Link] C38_C_0805_2012Metric_74cbd35bff10_ln_016  label="C31_C_0805_2012Metric_a2a63c8358cd"
  LinkPlacement = pos=(25.8,18.7,-1.6) rot=(0,1,0;3.14159rad)
  LinkedObject = -> Shape005
  Placement = pos=(25.8,18.7,-1.6) rot=(0,1,0;3.14159rad)
FEATURE [Part::Feature] Shape020  label="D7_D_SMC_a35920f9d814"
  Placement = pos=(20.55,23.216,-1.6) rot=(0.707107,-0.707107,0;3.14159rad)
  shape: bbox 5.9 x 8 x 2.31 mm, 41 faces (baked)
FEATURE [App::Link] J4_Broadcom_AFBR_16xxZ_Horizontal_9b6c4e7f7e3c_ln_001  label="J3_Broadcom_AFBR-16xxZ_Horizontal_92a701fb3616"
  LinkPlacement = pos=(11.2,74.504,-1.6) rot=(0,1,0;3.14159rad)
  LinkedObject = -> Shape013
  Placement = pos=(11.2,74.504,-1.6) rot=(0,1,0;3.14159rad)
FEATURE [App::Part] Bot_ed05
  Group = -> [Shape012,C38_C_0805_2012Metric_74cbd35bff10_ln_011,C15_C_0603_1608Metric_09ddd0478757_ln_019,C38_C_0805_2012Metric_74cbd35bff10_ln_012,Shape013,R21_R_0805_2012Metric_4eff570911b6_ln_011,CQ_assembly,Shape014,C38_C_0805_2012Metric_74cbd35bff10_ln_013,Shape015,R9_R_0603_1608Metric_fe9d9f34c5f9_ln_016,R9_R_0603_1608Metric_fe9d9f34c5f9_ln_017,J10_PinHeader_1x02_P254mm_Horizontal_7643f22ec726_ln_,+29 more]
  Origin = -> Origin004
FEATURE [App::Part] Step_Models_ed05
  Group = -> [Top_ed05,Bot_ed05]
  Origin = -> Origin002
FEATURE [App::Part] Board_ed05  label="HalfBridge_SiC"
  Group = -> [Local_CS_ed05,Board_Geoms_ed05,Step_Models_ed05]
  Origin = -> Origin001
COMPONENT P3 — same part as P2; its construction recipe is shown at P2.
COMPONENT P4 — recipe-attached ("Rectifier", a linked part whose construction recipe lives in a companion FreeCAD document of the same project; that document's serialized recipe follows).
Construction recipe (the companion document, serialized — sketch geometry with constraints, then the solid features built on it; lengths are millimeters unless a unit is written):

FCSTD DOCUMENT  (FreeCAD 1.0R39109 (Git))
Label: Rectifier
License: All rights reserved
LicenseURL: https://en.wikipedia.org/wiki/All_rights_reserved
objects: Part::Feature×35, App::Part×15, App::Link×6, PartDesign::CoordinateSystem×1, Sketcher::SketchObject×1
note: 38 computed .brp shape members not serialized (recipe doc carries the construction recipe); baked Part::Feature solids carry a one-line shape summary decoded from their .brp

FEATURE [Part::Feature] Part__Feature  label="Terminals4T"
  Placement = pos=(0,0,0.05) rot=(0,0,1;0rad)
  shape: bbox 5.8 x 4 x 9.3 mm, 23 faces (baked)
FEATURE [Part::Feature] Part__Feature001  label="Terminals4T001"
  Placement = pos=(0,0,0.05) rot=(0,0,1;0rad)
  shape: bbox 5.464 x 6.323 x 9.3 mm, 23 faces (baked)
FEATURE [Part::Feature] Part__Feature002  label="Terminals4T002"
  Placement = pos=(0,0,0.05) rot=(0,0,1;0rad)
  shape: bbox 5.464 x 6.323 x 9.3 mm, 23 faces (baked)
FEATURE [Part::Feature] Part__Feature003  label="Terminals4T003"
  Placement = pos=(0,0,0.05) rot=(0,0,1;0rad)
  shape: bbox 5.8 x 4 x 9.3 mm, 23 faces (baked)
FEATURE [App::Part] Terminals4T  label="Terminals4T004"
  Group = -> [Part__Feature,Part__Feature001,Part__Feature002,Part__Feature003]
  Origin = -> Origin008
FEATURE [Part::Feature] Part__Feature004  label="PCBHoles4T"
  Placement = pos=(0,0,0.95) rot=(0,0,1;0rad)
  shape: bbox 2.1 x 2.1 x 1.6 mm, 4 faces (baked)
FEATURE [Part::Feature] Part__Feature005  label="PCBHoles4T001"
  Placement = pos=(0,0,0.95) rot=(0,0,1;0rad)
  shape: bbox 2.1 x 2.1 x 1.6 mm, 4 faces (baked)
FEATURE [Part::Feature] Part__Feature006  label="PCBHoles4T002"
  Placement = pos=(0,0,0.95) rot=(0,0,1;0rad)
  shape: bbox 2.1 x 2.1 x 1.6 mm, 4 faces (baked)
FEATURE [Part::Feature] Part__Feature007  label="PCBHoles4T003"
  Placement = pos=(0,0,0.95) rot=(0,0,1;0rad)
  shape: bbox 2.1 x 2.1 x 1.6 mm, 4 faces (baked)
FEATURE [App::Part] PCBHoles4T  label="PCBHoles4T004"
  Group = -> [Part__Feature004,Part__Feature005,Part__Feature006,Part__Feature007]
  Origin = -> Origin009
FEATURE [Part::Feature] Part__Feature008  label="Disc"
  shape: bbox 30.3 x 30.3 x 0.01 mm, 3 faces (baked)
FEATURE [Part::Feature] Part__Feature009  label="BottomInsulation"
  Placement = pos=(0,0,-80.95) rot=(1,0,0;3.14159rad)
  shape: bbox 28.8 x 28.8 x 0.01 mm, 3 faces (baked)
FEATURE [Part::Feature] Part__Feature010  label="Can3D"
  shape: bbox 39.62 x 39.62 x 82 mm, 13 faces (baked)
FEATURE [Part::Feature] Part__Feature011  label="InkMinusBar"
  shape: bbox 19.54 x 26.11 x 82.1 mm, 51 faces (baked)
FEATURE [Part::Feature] Part__Feature012  label="InkLogo"
  shape: bbox 2.7 x 18 x 4.509 mm, 8 faces (baked)
FEATURE [Part::Feature] Part__Feature013  label="InkLogo001"
  shape: bbox 4.05 x 17.81 x 4.5 mm, 13 faces (baked)
FEATURE [Part::Feature] Part__Feature014  label="InkLogo002"
  shape: bbox 0.9 x 17.48 x 4.5 mm, 6 faces (baked)
FEATURE [Part::Feature] Part__Feature015  label="InkLogo003"
  shape: bbox 10.67 x 18.05 x 9.237 mm, 6 faces (baked)
FEATURE [Part::Feature] Part__Feature016  label="InkLogo004"
  shape: bbox 3.6 x 17 x 4.5 mm, 11 faces (baked)
FEATURE [Part::Feature] Part__Feature017  label="InkLogo005"
  shape: bbox 23.79 x 18.05 x 5.447 mm, 6 faces (baked)
FEATURE [Part::Feature] Part__Feature018  label="InkLogo006"
  shape: bbox 3.6 x 17 x 4.5 mm, 10 faces (baked)
FEATURE [Part::Feature] Part__Feature019  label="InkLogo007"
  shape: bbox 3.6 x 18.05 x 4.5 mm, 14 faces (baked)
FEATURE [App::Part] InkLogo  label="InkLogo008"
  Group = -> [Part__Feature012,Part__Feature013,Part__Feature014,Part__Feature015,Part__Feature016,Part__Feature017,Part__Feature018,Part__Feature019]
  Origin = -> Origin010
FEATURE [App::Part] ASSEMBLY  label="C1_ASSEMBLY_b2b269c604fa"
  Group = -> [Terminals4T,PCBHoles4T,Part__Feature008,Part__Feature009,Part__Feature010,Part__Feature011,InkLogo]
  Origin = -> Origin011
  Placement = pos=(79.248,61.214,2.5) rot=(0.707107,0.707107,0;3.14159rad)
FEATURE [App::Link] C1_ASSEMBLY_b2b269c604fa_ln_  label="C2_ASSEMBLY_92221c3fffa6"
  LinkPlacement = pos=(79.248,25.014,2.5) rot=(0.707107,0.707107,0;3.14159rad)
  LinkedObject = -> ASSEMBLY
  Placement = pos=(79.248,25.014,2.5) rot=(0.707107,0.707107,0;3.14159rad)
FEATURE [App::Link] C1_ASSEMBLY_b2b269c604fa_ln_001  label="C4_ASSEMBLY_e54dfc858ab3"
  LinkPlacement = pos=(43.148,25.014,2.5) rot=(0.707107,0.707107,0;3.14159rad)
  LinkedObject = -> ASSEMBLY
  Placement = pos=(43.148,25.014,2.5) rot=(0.707107,0.707107,0;3.14159rad)
FEATURE [Part::Feature] Part__Feature020  label="Diode_Bridge_IXYS_GUFP"
  shape: bbox 5.5 x 35 x 25 mm, 12 faces (baked)
FEATURE [Part::Feature] Part__Feature021  label="Diode_Bridge_IXYS_GUFP001"
  shape: bbox 0.5 x 2 x 20.4 mm, 12 faces (baked)
FEATURE [Part::Feature] Part__Feature022  label="Diode_Bridge_IXYS_GUFP002"
  shape: bbox 0.5 x 2 x 20.4 mm, 12 faces (baked)
FEATURE [Part::Feature] Part__Feature023  label="Diode_Bridge_IXYS_GUFP003"
  shape: bbox 0.5 x 2 x 20.4 mm, 12 faces (baked)
FEATURE [Part::Feature] Part__Feature024  label="Diode_Bridge_IXYS_GUFP004"
  shape: bbox 0.5 x 2 x 20.4 mm, 12 faces (baked)
FEATURE [Part::Feature] Part__Feature025  label="Diode_Bridge_IXYS_GUFP005"
  shape: bbox 0.5 x 2 x 20.4 mm, 12 faces (baked)
FEATURE [App::Part] Diode_Bridge_IXYS_GUFP  label="D1_Diode_Bridge_IXYS_GUFP006_09235a4c6129"
  Group = -> [Part__Feature020,Part__Feature021,Part__Feature022,Part__Feature023,Part__Feature024,Part__Feature025]
  Origin = -> Origin012
  Placement = pos=(22.836,57.432,0) rot=(0,0,1;0rad)
FEATURE [App::Link] C1_ASSEMBLY_b2b269c604fa_ln_002  label="C3_ASSEMBLY_94673b4dca56"
  LinkPlacement = pos=(43.148,61.214,2.5) rot=(0.707107,0.707107,0;3.14159rad)
  LinkedObject = -> ASSEMBLY
  Placement = pos=(43.148,61.214,2.5) rot=(0.707107,0.707107,0;3.14159rad)
FEATURE [App::Part] Top_47f8
  Group = -> [ASSEMBLY,C1_ASSEMBLY_b2b269c604fa_ln_,C1_ASSEMBLY_b2b269c604fa_ln_001,Diode_Bridge_IXYS_GUFP,C1_ASSEMBLY_b2b269c604fa_ln_002]
  Origin = -> Origin003
FEATURE [Part::Feature] Shape  label="R2_R_Axial_DIN0617_L170mm_D60mm_P3048mm_Horizontal_df3f5ee40b8e"
  Placement = pos=(61.0507,41.439,-1.6) rot=(0.707107,-0.707107,0;3.14159rad)
  shape: bbox 6.494 x 31.54 x 9.247 mm, 17 faces (baked)
FEATURE [Part::Feature] Shape001  label="J3_1_837fcd1c15ac[2]"
  Placement = pos=(96.48,44.12,-1.6) rot=(0.707107,-0.707107,0;3.14159rad)
  shape: bbox 7 x 4.98 x 4.98 mm, 13 faces (baked)
FEATURE [App::Link] J3_1_837fcd1c15ac_2__ln_  label="J4_1_bd25680a7361[2]"
  LinkPlacement = pos=(96.48,64.44,-1.6) rot=(0.707107,-0.707107,0;3.14159rad)
  LinkedObject = -> Shape001
  Placement = pos=(96.48,64.44,-1.6) rot=(0.707107,-0.707107,0;3.14159rad)
FEATURE [App::Link] R2_R_Axial_DIN0617_L170mm_D60mm_P3048mm_Horizontal_df3f5ee40b8e_ln_  label="R1_R_Axial_DIN0617_L170mm_D60mm_P3048mm_Horizontal_cec914eaf409"
  LinkPlacement = pos=(61.0507,74.967,-1.6) rot=(0.707107,-0.707107,0;3.14159rad)
  LinkedObject = -> Shape
  Placement = pos=(61.0507,74.967,-1.6) rot=(0.707107,-0.707107,0;3.14159rad)
FEATURE [Part::Feature] Part__Feature026  label="b6d24482-a09d-11ed-8f45-a0cec80452fd_part"
  shape: bbox 39.3 x 24.15 x 19.6 mm, 50 faces (baked)
FEATURE [App::Part] b6d24482_a09d_11ed_8f45_a0cec80452fd  label="b6d24482-a09d-11ed-8f45-a0cec80452fd"
  Group = -> [Part__Feature026]
  Origin = -> Origin013
FEATURE [Part::Feature] Part__Feature027  label="b6d2475c-a09d-11ed-8f45-a0cec80452fd_part"
  shape: bbox 2.1 x 2.1 x 4.6 mm, 8 faces (baked)
FEATURE [Part::Feature] Part__Feature028  label="b6d2475c-a09d-11ed-8f45-a0cec80452fd_part001"
  shape: bbox 2.1 x 2.1 x 4.6 mm, 8 faces (baked)
FEATURE [Part::Feature] Part__Feature029  label="b6d2475c-a09d-11ed-8f45-a0cec80452fd_part002"
  shape: bbox 2.1 x 2.1 x 4.6 mm, 8 faces (baked)
FEATURE [Part::Feature] Part__Feature030  label="b6d2475c-a09d-11ed-8f45-a0cec80452fd_part003"
  shape: bbox 2.1 x 2.1 x 4.6 mm, 8 faces (baked)
FEATURE [Part::Feature] Part__Feature031  label="b6d2475c-a09d-11ed-8f45-a0cec80452fd_part004"
  shape: bbox 2.1 x 2.1 x 4.6 mm, 8 faces (baked)
FEATURE [App::Part] b6d2475c_a09d_11ed_8f45_a0cec80452fd_part  label="b6d2475c-a09d-11ed-8f45-a0cec80452fd_part005"
  Group = -> [Part__Feature027,Part__Feature028,Part__Feature029,Part__Feature030,Part__Feature031]
  Origin = -> Origin014
FEATURE [App::Part] b6d2475c_a09d_11ed_8f45_a0cec80452fd  label="b6d2475c-a09d-11ed-8f45-a0cec80452fd"
  Group = -> [b6d2475c_a09d_11ed_8f45_a0cec80452fd_part]
  Origin = -> Origin015
FEATURE [App::Part] b6d2402c_a09d_11ed_8f45_a0cec80452fd  label="b6d2402c-a09d-11ed-8f45-a0cec80452fd"
  Group = -> [b6d24482_a09d_11ed_8f45_a0cec80452fd,b6d2475c_a09d_11ed_8f45_a0cec80452fd]
  Origin = -> Origin016
FEATURE [App::Part] CQ_assembly  label="J1_CQ assembly_da4fc33ca4ea"
  Group = -> [b6d2402c_a09d_11ed_8f45_a0cec80452fd]
  Origin = -> Origin017
  Placement = pos=(15.672,31.444,-1.6) rot=(0.707107,0.707107,0;3.14159rad)
FEATURE [App::Link] J3_1_837fcd1c15ac_2__ln_001  label="J2_1_f1523509d322[2]"
  LinkPlacement = pos=(96.48,23.8,-1.6) rot=(0.707107,-0.707107,0;3.14159rad)
  LinkedObject = -> Shape001
  Placement = pos=(96.48,23.8,-1.6) rot=(0.707107,-0.707107,0;3.14159rad)
FEATURE [App::Part] Bot_47f8
  Group = -> [Shape,Shape001,J3_1_837fcd1c15ac_2__ln_,R2_R_Axial_DIN0617_L170mm_D60mm_P3048mm_Horizontal_df3f5ee40b8e_ln_,CQ_assembly,J3_1_837fcd1c15ac_2__ln_001]
  Origin = -> Origin004
FEATURE [App::Part] Step_Models_47f8
  Group = -> [Top_47f8,Bot_47f8]
  Origin = -> Origin002
FEATURE [PartDesign::CoordinateSystem] Local_CS_47f8
  AttacherType = Attacher::AttachEngine3D
  MapMode = 2
FEATURE [Part::Feature] Pcb_47f8
  Placement = pos=(-53.67,129.248,0) rot=(0,0,1;0rad)
  shape: bbox 100 x 100 x 1.6 mm, 41 faces (baked)
FEATURE [Sketcher::SketchObject] PCB_Sketch_47f8
  ArcFitTolerance = 1e-06
  FullyConstrained = false
  MakeInternals = false
  sketch-geometry (4):
    g0: LineSegment StartX=0 StartY=100 StartZ=0 EndX=100 EndY=100 EndZ=0
    g1: LineSegment StartX=100 StartY=100 StartZ=0 EndX=100 EndY=0 EndZ=0
    g2: LineSegment StartX=100 StartY=0 StartZ=0 EndX=0 EndY=0 EndZ=0
    g3: LineSegment StartX=0 StartY=0 StartZ=0 EndX=0 EndY=100 EndZ=0
  constraints (4):
    c: Coincident(g2,g3)
    c: Coincident(g0,g3)
    c: Coincident(g1,g2)
    c: Coincident(g0,g1)
FEATURE [App::Part] Board_Geoms_47f8
  Group = -> [Pcb_47f8,PCB_Sketch_47f8]
  Origin = -> Origin
FEATURE [App::Part] Board_47f8  label="Rectifier"
  Group = -> [Step_Models_47f8,Local_CS_47f8,Board_Geoms_47f8]
  Origin = -> Origin001
PROVENANCE & LICENSES
A FreeCAD (.FCStd) document from a public repository crawl; recipes are the document's own serialized feature recipes (and, for linked parts, companion documents' recipes).
License: as declared in the source repository (recorded in the dataset sidecar).
